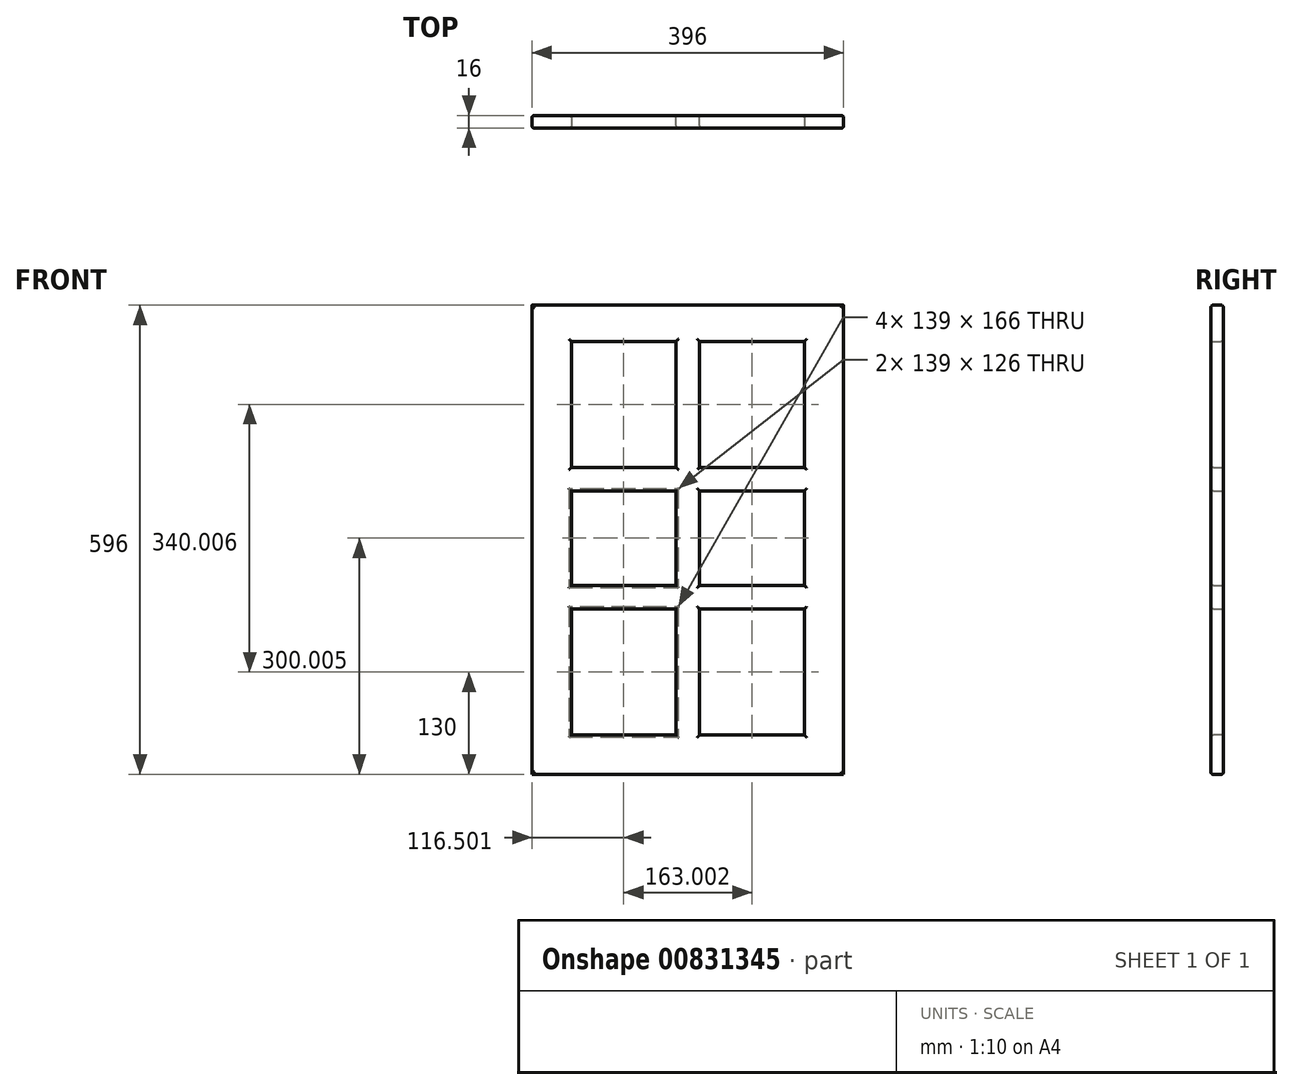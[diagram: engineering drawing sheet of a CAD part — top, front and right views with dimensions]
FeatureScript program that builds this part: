
annotation { "Feature Type Name" : "Feature", "Feature Type Description" : "" }
export const myFeature = defineFeature(function(context is Context, id is Id, definition is map)
    precondition{}
    {
        {
            var Q0;
            Q0=qCreatedBy(makeId("Front.planeOp"),FACE);
            var sketch = newSketch(context, id + "F0", { "sketchPlane" : qUnion([Q0])});
            skLineSegment(sketch, "E0.bottom", {"start": v(0, 0) * mm, "end": v(28.85, 0) * mm});
            skLineSegment(sketch, "E0.top", {"start": v(0, 37.88) * mm, "end": v(28.85, 37.88) * mm});
            skLineSegment(sketch, "E0.left", {"start": v(0, 0) * mm, "end": v(0, 37.88) * mm});
            skLineSegment(sketch, "E0.right", {"start": v(28.85, 0) * mm, "end": v(28.85, 37.88) * mm});
            skSolve(sketch);
        }
        {
            var Q0;
            Q0=makeQuery(id+"F0.imprint","IMPRINT",FACE,{"disambiguationData":[TD([[makeQuery(id+"F0.imprint","IMPRINT",EDGE,{"derivedFrom":sQuery(id+"F0.wireOp",EDGE,"E0.bottom")}),1.0]])]});
            extrude(context, id + "F1", {"entities" : qUnion([Q0]), "depth" : 16 * mm, "offsetDistance" : 25.4 * mm});
        }
        {
            var Q0;
            Q0=makeQuery(id+"F1.opExtrude","SWEPT_FACE",FACE,{"disambiguationData":[OSD([sQuery(id+"F0.wireOp",EDGE,"E0.left")])]});
            extrude(context, id + "F2", {"entities" : qUnion([Q0]), "operationType" : NewBodyOperationType.ADD, "oppositeDirection" : true, "depth" : 296 * mm, "offsetDistance" : 25.4 * mm});
        }
        {
            var Q0;
            {var subQ0=sQuery(id+"F0.wireOp",EDGE,"E0.bottom");Q0=makeQuery(id+"F2.boolean.opBoolean","MERGE",FACE,{"derivedFrom":[makeQuery(id+"F1.opExtrude","SWEPT_FACE",FACE,{"disambiguationData":[OSD([subQ0])]}),makeQuery(id+"F2.opExtrude","SWEPT_FACE",FACE,{"disambiguationData":[OSD([subQ0,sQuery(id+"F0.wireOp",EDGE,"E0.left")])]})]});}
            extrude(context, id + "F3", {"entities" : qUnion([Q0]), "operationType" : NewBodyOperationType.ADD, "oppositeDirection" : true, "depth" : 996 * mm, "offsetDistance" : 25 * mm});
        }
        {
            var Q0;
            {var subQ0=sQuery(id+"F0.wireOp",EDGE,"E0.left");var subQ1=sQuery(id+"F0.wireOp",EDGE,"E0.bottom");Q0=makeQuery(id+"F3.boolean.opBoolean","MERGE",FACE,{"derivedFrom":[makeQuery(id+"F2.boolean.opBoolean","MERGE",FACE,{"derivedFrom":[makeQuery(id+"F1.opExtrude","CAP_FACE",FACE,{"disambiguationData":[OSD([subQ1,sQuery(id+"F0.wireOp",EDGE,"E0.top"),subQ0,sQuery(id+"F0.wireOp",EDGE,"E0.right")])],"isStart":false}),makeQuery(id+"F2.opExtrude","SWEPT_FACE",FACE,{"disambiguationData":[OSD([subQ0]),TDD([makeQuery(id+"F1.opExtrude","CAP_EDGE",EDGE,{"disambiguationData":[OSD([subQ0])],"isStart":false})])]})]}),makeQuery(id+"F3.opExtrude","SWEPT_FACE",FACE,{"disambiguationData":[OSD([subQ1,subQ0]),TDD([makeQuery(id+"F2.boolean.opBoolean","MERGE",EDGE,{"derivedFrom":[makeQuery(id+"F1.opExtrude","CAP_EDGE",EDGE,{"disambiguationData":[OSD([subQ1])],"isStart":false}),makeQuery(id+"F2.opExtrude","SWEPT_EDGE",EDGE,{"disambiguationData":[OSD([subQ1,subQ0]),TDD([makeQuery(id+"F1.opExtrude","CAP_VERTEX",VERTEX,{"disambiguationData":[OSD([subQ1,subQ0])],"isStart":false})])]})]})])]})]});}
            var sketch = newSketch(context, id + "F4", { "sketchPlane" : qUnion([Q0])});
            skLineSegment(sketch, "E1.bottom", {"start": v(48.4, 906.79) * mm, "end": v(248.24, 906.79) * mm});
            skLineSegment(sketch, "E1.top", {"start": v(48.4, 105.66) * mm, "end": v(248.24, 105.66) * mm});
            skLineSegment(sketch, "E1.left", {"start": v(48.4, 906.79) * mm, "end": v(48.4, 105.66) * mm});
            skLineSegment(sketch, "E1.right", {"start": v(248.24, 906.79) * mm, "end": v(248.24, 105.66) * mm});
            skSolve(sketch);
        }
        {
            var Q0;
            Q0=makeQuery(id+"F4.imprint","IMPRINT",FACE,{"disambiguationData":[TD([[makeQuery(id+"F4.imprint","IMPRINT",EDGE,{"derivedFrom":sQuery(id+"F4.wireOp",EDGE,"E1.bottom")}),-1.0]])]});
            extrude(context, id + "F5", {"entities" : qUnion([Q0]), "operationType" : NewBodyOperationType.REMOVE, "oppositeDirection" : true, "depth" : 5 * mm, "offsetDistance" : 25 * mm});
        }
        {
            var Q0;
            Q0=makeQuery(id+"F5.boolean.opBoolean","COPY",FACE,{"derivedFrom":makeQuery(id+"F5.opExtrude","SWEPT_FACE",FACE,{"disambiguationData":[OSD([sQuery(id+"F4.wireOp",EDGE,"E1.bottom")])]})});
            extrude(context, id + "F6", {"entities" : qUnion([Q0]), "operationType" : NewBodyOperationType.REMOVE, "oppositeDirection" : true, "depth" : 39.2 * mm, "offsetDistance" : 25 * mm});
        }
        {
            var Q0;
            {var subQ0=sQuery(id+"F4.wireOp",EDGE,"E1.right");Q0=makeQuery(id+"F6.boolean.opBoolean","MERGE",FACE,{"derivedFrom":[makeQuery(id+"F5.boolean.opBoolean","COPY",FACE,{"derivedFrom":makeQuery(id+"F5.opExtrude","SWEPT_FACE",FACE,{"disambiguationData":[OSD([subQ0])]})}),makeQuery(id+"F6.opExtrude","SWEPT_FACE",FACE,{"disambiguationData":[OSD([sQuery(id+"F4.wireOp",EDGE,"E1.bottom"),subQ0])]})]});}
            extrude(context, id + "F7", {"entities" : qUnion([Q0]), "operationType" : NewBodyOperationType.ADD, "depth" : 2.24 * mm, "offsetDistance" : 25 * mm});
        }
        {
            var Q0;
            Q0=makeQuery(id+"F5.boolean.opBoolean","COPY",FACE,{"derivedFrom":makeQuery(id+"F5.opExtrude","SWEPT_FACE",FACE,{"disambiguationData":[OSD([sQuery(id+"F4.wireOp",EDGE,"E1.top")])]})});
            extrude(context, id + "F8", {"entities" : qUnion([Q0]), "operationType" : NewBodyOperationType.REMOVE, "oppositeDirection" : true, "depth" : 55.66 * mm, "offsetDistance" : 25 * mm});
        }
        {
            var Q0;
            {var subQ0=sQuery(id+"F4.wireOp",EDGE,"E1.left");Q0=makeQuery(id+"F8.boolean.opBoolean","MERGE",FACE,{"derivedFrom":[makeQuery(id+"F6.boolean.opBoolean","MERGE",FACE,{"derivedFrom":[makeQuery(id+"F5.boolean.opBoolean","COPY",FACE,{"derivedFrom":makeQuery(id+"F5.opExtrude","SWEPT_FACE",FACE,{"disambiguationData":[OSD([subQ0])]})}),makeQuery(id+"F6.opExtrude","SWEPT_FACE",FACE,{"disambiguationData":[OSD([sQuery(id+"F4.wireOp",EDGE,"E1.bottom"),subQ0])]})]}),makeQuery(id+"F8.opExtrude","SWEPT_FACE",FACE,{"disambiguationData":[OSD([sQuery(id+"F4.wireOp",EDGE,"E1.top"),subQ0])]})]});}
            extrude(context, id + "F9", {"entities" : qUnion([Q0]), "operationType" : NewBodyOperationType.ADD, "depth" : 1.59 * mm, "offsetDistance" : 25 * mm});
        }
        {
            var Q0;
            {var subQ0=sQuery(id+"F4.wireOp",EDGE,"E1.top");var subQ1=sQuery(id+"F4.wireOp",EDGE,"E1.bottom");Q0=makeQuery(id+"F8.boolean.opBoolean","MERGE",FACE,{"derivedFrom":[makeQuery(id+"F6.boolean.opBoolean","MERGE",FACE,{"derivedFrom":[makeQuery(id+"F5.boolean.opBoolean","COPY",FACE,{"derivedFrom":makeQuery(id+"F5.opExtrude","CAP_FACE",FACE,{"disambiguationData":[OSD([subQ1,subQ0,sQuery(id+"F4.wireOp",EDGE,"E1.left"),sQuery(id+"F4.wireOp",EDGE,"E1.right")])],"isStart":false})}),makeQuery(id+"F6.opExtrude","SWEPT_FACE",FACE,{"disambiguationData":[OSD([subQ1]),TDD([makeQuery(id+"F5.boolean.opBoolean","COPY",EDGE,{"derivedFrom":makeQuery(id+"F5.opExtrude","CAP_EDGE",EDGE,{"disambiguationData":[OSD([subQ1])],"isStart":false})})])]})]}),makeQuery(id+"F8.opExtrude","SWEPT_FACE",FACE,{"disambiguationData":[OSD([subQ0]),TDD([makeQuery(id+"F5.boolean.opBoolean","COPY",EDGE,{"derivedFrom":makeQuery(id+"F5.opExtrude","CAP_EDGE",EDGE,{"disambiguationData":[OSD([subQ0])],"isStart":false})})])]})]});}
            var sketch = newSketch(context, id + "F10", { "sketchPlane" : qUnion([Q0])});
            skLineSegment(sketch, "E2.bottom", {"start": v(127.14, 946) * mm, "end": v(181.91, 946) * mm});
            skLineSegment(sketch, "E2.top", {"start": v(127.14, 50) * mm, "end": v(181.91, 50) * mm});
            skLineSegment(sketch, "E2.left", {"start": v(127.14, 946) * mm, "end": v(127.14, 50) * mm});
            skLineSegment(sketch, "E2.right", {"start": v(181.91, 946) * mm, "end": v(181.91, 50) * mm});
            skSolve(sketch);
        }
        {
            var Q0;
            Q0=makeQuery(id+"F10.imprint","IMPRINT",FACE,{"disambiguationData":[TD([[makeQuery(id+"F10.imprint","IMPRINT",EDGE,{"derivedFrom":sQuery(id+"F10.wireOp",EDGE,"E2.bottom")}),-1.0]])]});
            extrude(context, id + "F11", {"entities" : qUnion([Q0]), "operationType" : NewBodyOperationType.ADD, "depth" : 5 * mm, "offsetDistance" : 25 * mm});
        }
        {
            var Q0;
            Q0=makeQuery(id+"F11.opExtrude","SWEPT_FACE",FACE,{"disambiguationData":[OSD([sQuery(id+"F10.wireOp",EDGE,"E2.left")])]});
            extrude(context, id + "F12", {"entities" : qUnion([Q0]), "operationType" : NewBodyOperationType.REMOVE, "oppositeDirection" : true, "depth" : 5.86 * mm, "offsetDistance" : 25 * mm});
        }
        {
            var Q0;
            Q0=makeQuery(id+"F11.opExtrude","SWEPT_FACE",FACE,{"disambiguationData":[OSD([sQuery(id+"F10.wireOp",EDGE,"E2.right")])]});
            extrude(context, id + "F13", {"entities" : qUnion([Q0]), "operationType" : NewBodyOperationType.REMOVE, "oppositeDirection" : true, "depth" : 18.91 * mm, "offsetDistance" : 25 * mm});
        }
        {
            var Q0;
            {var subQ0=sQuery(id+"F10.wireOp",EDGE,"E2.left");var subQ1=sQuery(id+"F4.wireOp",EDGE,"E1.bottom");var subQ2=sQuery(id+"F4.wireOp",EDGE,"E1.top");var subQ3=sQuery(id+"F4.wireOp",EDGE,"E1.left");Q0=makeQuery(id+"F12.boolean.opBoolean","MERGE",FACE,{"derivedFrom":[makeQuery(id+"F11.boolean.opBoolean","SPLIT",FACE,{"disambiguationData":[TD([makeQuery(id+"F11.opExtrude","SWEPT_FACE",FACE,{"disambiguationData":[OSD([subQ0])]})])],"derivedFrom":makeQuery(id+"F8.boolean.opBoolean","MERGE",FACE,{"derivedFrom":[makeQuery(id+"F6.boolean.opBoolean","MERGE",FACE,{"derivedFrom":[makeQuery(id+"F5.boolean.opBoolean","COPY",FACE,{"derivedFrom":makeQuery(id+"F5.opExtrude","CAP_FACE",FACE,{"disambiguationData":[OSD([subQ1,subQ2,subQ3,sQuery(id+"F4.wireOp",EDGE,"E1.right")])],"isStart":false})}),makeQuery(id+"F6.opExtrude","SWEPT_FACE",FACE,{"disambiguationData":[OSD([subQ1]),TDD([makeQuery(id+"F5.boolean.opBoolean","COPY",EDGE,{"derivedFrom":makeQuery(id+"F5.opExtrude","CAP_EDGE",EDGE,{"disambiguationData":[OSD([subQ1])],"isStart":false})})])]})]}),makeQuery(id+"F8.opExtrude","SWEPT_FACE",FACE,{"disambiguationData":[OSD([subQ2]),TDD([makeQuery(id+"F5.boolean.opBoolean","COPY",EDGE,{"derivedFrom":makeQuery(id+"F5.opExtrude","CAP_EDGE",EDGE,{"disambiguationData":[OSD([subQ2])],"isStart":false})})])]})]})}),makeQuery(id+"F12.opExtrude","SWEPT_FACE",FACE,{"disambiguationData":[OSD([subQ0]),TDD([makeQuery(id+"F11.opExtrude","CAP_EDGE",EDGE,{"disambiguationData":[OSD([subQ0])],"isStart":true})])]})]});}
            var sketch = newSketch(context, id + "F14", { "sketchPlane" : qUnion([Q0])});
            skLineSegment(sketch, "E3.bottom", {"start": v(50, 870.78) * mm, "end": v(133, 870.78) * mm});
            skLineSegment(sketch, "E3.top", {"start": v(50, 835.83) * mm, "end": v(133, 835.83) * mm});
            skLineSegment(sketch, "E3.left", {"start": v(50, 870.78) * mm, "end": v(50, 835.83) * mm});
            skLineSegment(sketch, "E3.right", {"start": v(133, 870.78) * mm, "end": v(133, 835.83) * mm});
            skLineSegment(sketch, "E4.bottom", {"start": v(50, 539.3) * mm, "end": v(133, 539.3) * mm});
            skLineSegment(sketch, "E4.top", {"start": v(50, 484.02) * mm, "end": v(133, 484.02) * mm});
            skLineSegment(sketch, "E4.left", {"start": v(50, 539.3) * mm, "end": v(50, 484.02) * mm});
            skLineSegment(sketch, "E4.right", {"start": v(133, 539.3) * mm, "end": v(133, 484.02) * mm});
            skSolve(sketch);
        }
        {
            var Q0;
            {var subQ0=sQuery(id+"F10.wireOp",EDGE,"E2.right");var subQ1=sQuery(id+"F4.wireOp",EDGE,"E1.top");var subQ2=sQuery(id+"F4.wireOp",EDGE,"E1.right");var subQ3=sQuery(id+"F4.wireOp",EDGE,"E1.bottom");Q0=makeQuery(id+"F13.boolean.opBoolean","MERGE",FACE,{"derivedFrom":[makeQuery(id+"F11.boolean.opBoolean","SPLIT",FACE,{"disambiguationData":[TD([makeQuery(id+"F11.opExtrude","SWEPT_FACE",FACE,{"disambiguationData":[OSD([subQ0])]})])],"derivedFrom":makeQuery(id+"F8.boolean.opBoolean","MERGE",FACE,{"derivedFrom":[makeQuery(id+"F6.boolean.opBoolean","MERGE",FACE,{"derivedFrom":[makeQuery(id+"F5.boolean.opBoolean","COPY",FACE,{"derivedFrom":makeQuery(id+"F5.opExtrude","CAP_FACE",FACE,{"disambiguationData":[OSD([subQ3,subQ1,sQuery(id+"F4.wireOp",EDGE,"E1.left"),subQ2])],"isStart":false})}),makeQuery(id+"F6.opExtrude","SWEPT_FACE",FACE,{"disambiguationData":[OSD([subQ3]),TDD([makeQuery(id+"F5.boolean.opBoolean","COPY",EDGE,{"derivedFrom":makeQuery(id+"F5.opExtrude","CAP_EDGE",EDGE,{"disambiguationData":[OSD([subQ3])],"isStart":false})})])]})]}),makeQuery(id+"F8.opExtrude","SWEPT_FACE",FACE,{"disambiguationData":[OSD([subQ1]),TDD([makeQuery(id+"F5.boolean.opBoolean","COPY",EDGE,{"derivedFrom":makeQuery(id+"F5.opExtrude","CAP_EDGE",EDGE,{"disambiguationData":[OSD([subQ1])],"isStart":false})})])]})]})}),makeQuery(id+"F13.opExtrude","SWEPT_FACE",FACE,{"disambiguationData":[OSD([subQ0]),TDD([makeQuery(id+"F11.opExtrude","CAP_EDGE",EDGE,{"disambiguationData":[OSD([subQ0])],"isStart":true})])]})]});}
            var sketch = newSketch(context, id + "F15", { "sketchPlane" : qUnion([Q0])});
            skLineSegment(sketch, "E5.bottom", {"start": v(163, 876.14) * mm, "end": v(246, 876.14) * mm});
            skLineSegment(sketch, "E5.top", {"start": v(163, 831.26) * mm, "end": v(246, 831.26) * mm});
            skLineSegment(sketch, "E5.left", {"start": v(163, 876.14) * mm, "end": v(163, 831.26) * mm});
            skLineSegment(sketch, "E5.right", {"start": v(246, 876.14) * mm, "end": v(246, 831.26) * mm});
            skLineSegment(sketch, "E6.bottom", {"start": v(163, 602.8) * mm, "end": v(246, 602.8) * mm});
            skLineSegment(sketch, "E6.top", {"start": v(163, 550.28) * mm, "end": v(246, 550.28) * mm});
            skLineSegment(sketch, "E6.left", {"start": v(163, 602.8) * mm, "end": v(163, 550.28) * mm});
            skLineSegment(sketch, "E6.right", {"start": v(246, 602.8) * mm, "end": v(246, 550.28) * mm});
            skSolve(sketch);
        }
        {
            var Q0;
            Q0=makeQuery(id+"F14.imprint","IMPRINT",FACE,{"disambiguationData":[TD([[makeQuery(id+"F14.imprint","IMPRINT",EDGE,{"derivedFrom":sQuery(id+"F14.wireOp",EDGE,"E3.bottom")}),-1.0]])]});
            var Q1;
            Q1=makeQuery(id+"F15.imprint","IMPRINT",FACE,{"disambiguationData":[TD([[makeQuery(id+"F15.imprint","IMPRINT",EDGE,{"derivedFrom":sQuery(id+"F15.wireOp",EDGE,"E5.bottom")}),-1.0]])]});
            var Q2;
            Q2=makeQuery(id+"F15.imprint","IMPRINT",FACE,{"disambiguationData":[TD([[makeQuery(id+"F15.imprint","IMPRINT",EDGE,{"derivedFrom":sQuery(id+"F15.wireOp",EDGE,"E6.bottom")}),-1.0]])]});
            var Q3;
            Q3=makeQuery(id+"F14.imprint","IMPRINT",FACE,{"disambiguationData":[TD([[makeQuery(id+"F14.imprint","IMPRINT",EDGE,{"derivedFrom":sQuery(id+"F14.wireOp",EDGE,"E4.bottom")}),-1.0]])]});
            extrude(context, id + "F16", {"entities" : qUnion([Q0, Q1, Q2, Q3]), "operationType" : NewBodyOperationType.ADD, "depth" : 5 * mm, "offsetDistance" : 25 * mm});
        }
        {
            var Q0;
            Q0=makeQuery(id+"F16.opExtrude","SWEPT_FACE",FACE,{"disambiguationData":[OSD([sQuery(id+"F15.wireOp",EDGE,"E6.top")])]});
            var Q1;
            Q1=makeQuery(id+"F16.opExtrude","SWEPT_FACE",FACE,{"disambiguationData":[OSD([sQuery(id+"F14.wireOp",EDGE,"E4.top")])]});
            extrude(context, id + "F17", {"entities" : qUnion([Q0, Q1]), "operationType" : NewBodyOperationType.ADD, "depth" : 300 * mm, "offsetDistance" : 25 * mm});
        }
        {
            var Q0;
            Q0=makeQuery(id+"F16.opExtrude","SWEPT_FACE",FACE,{"disambiguationData":[OSD([sQuery(id+"F14.wireOp",EDGE,"E4.bottom")])]});
            var Q1;
            Q1=makeQuery(id+"F16.opExtrude","SWEPT_FACE",FACE,{"disambiguationData":[OSD([sQuery(id+"F15.wireOp",EDGE,"E6.bottom")])]});
            extrude(context, id + "F18", {"entities" : qUnion([Q0, Q1]), "operationType" : NewBodyOperationType.REMOVE, "oppositeDirection" : true, "depth" : 300 * mm, "offsetDistance" : 25 * mm});
        }
        {
            var Q0;
            Q0=makeQuery(id+"F16.opExtrude","SWEPT_FACE",FACE,{"disambiguationData":[OSD([sQuery(id+"F14.wireOp",EDGE,"E3.top")])]});
            extrude(context, id + "F19", {"entities" : qUnion([Q0]), "operationType" : NewBodyOperationType.ADD, "depth" : 324.8 * mm, "offsetDistance" : 25 * mm});
        }
        {
            var Q0;
            Q0=makeQuery(id+"F16.opExtrude","SWEPT_FACE",FACE,{"disambiguationData":[OSD([sQuery(id+"F14.wireOp",EDGE,"E3.bottom")])]});
            extrude(context, id + "F20", {"entities" : qUnion([Q0]), "operationType" : NewBodyOperationType.REMOVE, "oppositeDirection" : true, "depth" : 324.8 * mm, "offsetDistance" : 25 * mm});
        }
        {
            var Q0;
            Q0=makeQuery(id+"F18.boolean.opBoolean","COPY",FACE,{"derivedFrom":makeQuery(id+"F18.opExtrude","CAP_FACE",FACE,{"disambiguationData":[OSD([sQuery(id+"F14.wireOp",EDGE,"E4.bottom")])],"isStart":false})});
            extrude(context, id + "F21", {"entities" : qUnion([Q0]), "operationType" : NewBodyOperationType.ADD, "depth" : 250 * mm, "offsetDistance" : 25 * mm});
        }
        {
            var Q0;
            Q0=makeQuery(id+"F17.opExtrude","CAP_FACE",FACE,{"disambiguationData":[OSD([sQuery(id+"F14.wireOp",EDGE,"E4.top")])],"isStart":false});
            extrude(context, id + "F22", {"entities" : qUnion([Q0]), "operationType" : NewBodyOperationType.REMOVE, "oppositeDirection" : true, "depth" : 250 * mm, "offsetDistance" : 25 * mm});
        }
        {
            var Q0;
            Q0=makeQuery(id+"F20.boolean.opBoolean","COPY",FACE,{"derivedFrom":makeQuery(id+"F20.opExtrude","CAP_FACE",FACE,{"disambiguationData":[OSD([sQuery(id+"F14.wireOp",EDGE,"E3.bottom")])],"isStart":false})});
            extrude(context, id + "F23", {"entities" : qUnion([Q0]), "operationType" : NewBodyOperationType.ADD, "depth" : 100 * mm, "offsetDistance" : 25 * mm});
        }
        {
            var Q0;
            Q0=makeQuery(id+"F19.opExtrude","CAP_FACE",FACE,{"disambiguationData":[OSD([sQuery(id+"F14.wireOp",EDGE,"E3.top")])],"isStart":false});
            extrude(context, id + "F24", {"entities" : qUnion([Q0]), "operationType" : NewBodyOperationType.REMOVE, "oppositeDirection" : true, "depth" : 100 * mm, "offsetDistance" : 25 * mm});
        }
        {
            var Q0;
            Q0=makeQuery(id+"F23.opExtrude","CAP_FACE",FACE,{"disambiguationData":[OSD([sQuery(id+"F14.wireOp",EDGE,"E3.bottom")])],"isStart":false});
            extrude(context, id + "F25", {"entities" : qUnion([Q0]), "operationType" : NewBodyOperationType.ADD, "depth" : 50 * mm, "offsetDistance" : 25 * mm});
        }
        {
            var Q0;
            Q0=makeQuery(id+"F24.boolean.opBoolean","COPY",FACE,{"derivedFrom":makeQuery(id+"F24.opExtrude","CAP_FACE",FACE,{"disambiguationData":[OSD([sQuery(id+"F14.wireOp",EDGE,"E3.top")])],"isStart":false})});
            extrude(context, id + "F26", {"entities" : qUnion([Q0]), "operationType" : NewBodyOperationType.REMOVE, "oppositeDirection" : true, "depth" : 50 * mm, "offsetDistance" : 25 * mm});
        }
        {
            var Q0;
            Q0=makeQuery(id+"F22.boolean.opBoolean","COPY",FACE,{"derivedFrom":makeQuery(id+"F22.opExtrude","CAP_FACE",FACE,{"disambiguationData":[OSD([sQuery(id+"F14.wireOp",EDGE,"E4.top")])],"isStart":false})});
            extrude(context, id + "F27", {"entities" : qUnion([Q0]), "operationType" : NewBodyOperationType.ADD, "depth" : 134.02 * mm, "offsetDistance" : 25 * mm});
        }
        {
            var Q0;
            Q0=makeQuery(id+"F27.opExtrude","CAP_FACE",FACE,{"disambiguationData":[OSD([sQuery(id+"F14.wireOp",EDGE,"E4.top")])],"isStart":false});
            extrude(context, id + "F28", {"entities" : qUnion([Q0]), "operationType" : NewBodyOperationType.REMOVE, "oppositeDirection" : true, "depth" : 100 * mm, "offsetDistance" : 25 * mm});
        }
        {
            var Q0;
            Q0=makeQuery(id+"F26.boolean.opBoolean","COPY",FACE,{"derivedFrom":makeQuery(id+"F26.opExtrude","CAP_FACE",FACE,{"disambiguationData":[OSD([sQuery(id+"F14.wireOp",EDGE,"E3.top")])],"isStart":false})});
            extrude(context, id + "F29", {"entities" : qUnion([Q0]), "operationType" : NewBodyOperationType.ADD, "depth" : 100 * mm, "offsetDistance" : 25 * mm});
        }
        {
            var Q0;
            Q0=makeQuery(id+"F25.opExtrude","CAP_FACE",FACE,{"disambiguationData":[OSD([sQuery(id+"F14.wireOp",EDGE,"E3.bottom")])],"isStart":false});
            extrude(context, id + "F30", {"entities" : qUnion([Q0]), "operationType" : NewBodyOperationType.REMOVE, "oppositeDirection" : true, "depth" : 100 * mm, "offsetDistance" : 25 * mm});
        }
        {
            var Q0;
            Q0=makeQuery(id+"F30.boolean.opBoolean","COPY",FACE,{"derivedFrom":makeQuery(id+"F30.opExtrude","CAP_FACE",FACE,{"disambiguationData":[OSD([sQuery(id+"F14.wireOp",EDGE,"E3.bottom")])],"isStart":false})});
            extrude(context, id + "F31", {"entities" : qUnion([Q0]), "operationType" : NewBodyOperationType.ADD, "depth" : 50 * mm, "offsetDistance" : 25 * mm});
        }
        {
            var Q0;
            Q0=makeQuery(id+"F29.opExtrude","CAP_FACE",FACE,{"disambiguationData":[OSD([sQuery(id+"F14.wireOp",EDGE,"E3.top")])],"isStart":false});
            extrude(context, id + "F32", {"entities" : qUnion([Q0]), "operationType" : NewBodyOperationType.REMOVE, "oppositeDirection" : true, "depth" : 54.95 * mm, "offsetDistance" : 25 * mm});
        }
        {
            var Q0;
            Q0=makeQuery(id+"F28.boolean.opBoolean","COPY",FACE,{"derivedFrom":makeQuery(id+"F28.opExtrude","CAP_FACE",FACE,{"disambiguationData":[OSD([sQuery(id+"F14.wireOp",EDGE,"E4.top")])],"isStart":false})});
            extrude(context, id + "F33", {"entities" : qUnion([Q0]), "operationType" : NewBodyOperationType.ADD, "depth" : 50 * mm, "offsetDistance" : 25 * mm});
        }
        {
            var Q0;
            Q0=makeQuery(id+"F21.opExtrude","CAP_FACE",FACE,{"disambiguationData":[OSD([sQuery(id+"F14.wireOp",EDGE,"E4.bottom")])],"isStart":false});
            extrude(context, id + "F34", {"entities" : qUnion([Q0]), "operationType" : NewBodyOperationType.REMOVE, "oppositeDirection" : true, "depth" : 109.3 * mm, "offsetDistance" : 25 * mm});
        }
        {
            var Q0;
            Q0=makeQuery(id+"F16.opExtrude","SWEPT_FACE",FACE,{"disambiguationData":[OSD([sQuery(id+"F15.wireOp",EDGE,"E5.top")])]});
            extrude(context, id + "F35", {"entities" : qUnion([Q0]), "operationType" : NewBodyOperationType.REMOVE, "oppositeDirection" : true, "depth" : 14.88 * mm, "offsetDistance" : 25 * mm});
        }
        {
            var Q0;
            Q0=makeQuery(id+"F35.boolean.opBoolean","COPY",FACE,{"derivedFrom":makeQuery(id+"F35.opExtrude","CAP_FACE",FACE,{"disambiguationData":[OSD([sQuery(id+"F15.wireOp",EDGE,"E5.top")])],"isStart":false})});
            extrude(context, id + "F36", {"entities" : qUnion([Q0]), "operationType" : NewBodyOperationType.ADD, "depth" : 230.15 * mm, "offsetDistance" : 25 * mm});
        }
        {
            var Q0;
            Q0=makeQuery(id+"F16.opExtrude","SWEPT_FACE",FACE,{"disambiguationData":[OSD([sQuery(id+"F15.wireOp",EDGE,"E5.bottom")])]});
            extrude(context, id + "F37", {"entities" : qUnion([Q0]), "operationType" : NewBodyOperationType.REMOVE, "oppositeDirection" : true, "depth" : 230.15 * mm, "offsetDistance" : 25 * mm});
        }
        {
            var Q0;
            Q0=makeQuery(id+"F17.opExtrude","CAP_FACE",FACE,{"disambiguationData":[OSD([sQuery(id+"F15.wireOp",EDGE,"E6.top")])],"isStart":false});
            extrude(context, id + "F38", {"entities" : qUnion([Q0]), "operationType" : NewBodyOperationType.REMOVE, "oppositeDirection" : true, "depth" : 22.52 * mm, "offsetDistance" : 25 * mm});
        }
        {
            var Q0;
            Q0=makeQuery(id+"F18.boolean.opBoolean","COPY",FACE,{"derivedFrom":makeQuery(id+"F18.opExtrude","CAP_FACE",FACE,{"disambiguationData":[OSD([sQuery(id+"F15.wireOp",EDGE,"E6.bottom")])],"isStart":false})});
            extrude(context, id + "F39", {"entities" : qUnion([Q0]), "operationType" : NewBodyOperationType.ADD, "depth" : 77.2 * mm, "offsetDistance" : 25 * mm});
        }
        {
            var Q0;
            Q0=makeQuery(id+"F38.boolean.opBoolean","COPY",FACE,{"derivedFrom":makeQuery(id+"F38.opExtrude","CAP_FACE",FACE,{"disambiguationData":[OSD([sQuery(id+"F15.wireOp",EDGE,"E6.top")])],"isStart":false})});
            extrude(context, id + "F40", {"entities" : qUnion([Q0]), "operationType" : NewBodyOperationType.REMOVE, "oppositeDirection" : true, "depth" : 77.2 * mm, "offsetDistance" : 25 * mm});
        }
        {
            var Q0;
            {var subQ0=sQuery(id+"F14.wireOp",EDGE,"E3.bottom");var subQ1=makeQuery(id+"F16.opExtrude","CAP_EDGE",EDGE,{"disambiguationData":[OSD([subQ0])],"isStart":true});var subQ2=sQuery(id+"F10.wireOp",EDGE,"E2.left");var subQ3=sQuery(id+"F4.wireOp",EDGE,"E1.bottom");var subQ4=sQuery(id+"F4.wireOp",EDGE,"E1.left");var subQ5=sQuery(id+"F4.wireOp",EDGE,"E1.top");var subQ7=makeQuery(id+"F6.boolean.opBoolean","COPY",FACE,{"derivedFrom":makeQuery(id+"F6.opExtrude","CAP_FACE",FACE,{"disambiguationData":[OSD([subQ3])],"isStart":false})});Q0=makeQuery(id+"F30.boolean.opBoolean","MERGE",FACE,{"derivedFrom":[makeQuery(id+"F20.boolean.opBoolean","MERGE",FACE,{"derivedFrom":[makeQuery(id+"F16.boolean.opBoolean","SPLIT",FACE,{"disambiguationData":[TD([subQ7])],"derivedFrom":makeQuery(id+"F12.boolean.opBoolean","MERGE",FACE,{"derivedFrom":[makeQuery(id+"F11.boolean.opBoolean","SPLIT",FACE,{"disambiguationData":[TD([makeQuery(id+"F11.opExtrude","SWEPT_FACE",FACE,{"disambiguationData":[OSD([subQ2])]})])],"derivedFrom":makeQuery(id+"F8.boolean.opBoolean","MERGE",FACE,{"derivedFrom":[makeQuery(id+"F6.boolean.opBoolean","MERGE",FACE,{"derivedFrom":[makeQuery(id+"F5.boolean.opBoolean","COPY",FACE,{"derivedFrom":makeQuery(id+"F5.opExtrude","CAP_FACE",FACE,{"disambiguationData":[OSD([subQ3,subQ5,subQ4,sQuery(id+"F4.wireOp",EDGE,"E1.right")])],"isStart":false})}),makeQuery(id+"F6.opExtrude","SWEPT_FACE",FACE,{"disambiguationData":[OSD([subQ3]),TDD([makeQuery(id+"F5.boolean.opBoolean","COPY",EDGE,{"derivedFrom":makeQuery(id+"F5.opExtrude","CAP_EDGE",EDGE,{"disambiguationData":[OSD([subQ3])],"isStart":false})})])]})]}),makeQuery(id+"F8.opExtrude","SWEPT_FACE",FACE,{"disambiguationData":[OSD([subQ5]),TDD([makeQuery(id+"F5.boolean.opBoolean","COPY",EDGE,{"derivedFrom":makeQuery(id+"F5.opExtrude","CAP_EDGE",EDGE,{"disambiguationData":[OSD([subQ5])],"isStart":false})})])]})]})}),makeQuery(id+"F12.opExtrude","SWEPT_FACE",FACE,{"disambiguationData":[OSD([subQ2]),TDD([makeQuery(id+"F11.opExtrude","CAP_EDGE",EDGE,{"disambiguationData":[OSD([subQ2])],"isStart":true})])]})]})}),makeQuery(id+"F20.opExtrude","SWEPT_FACE",FACE,{"disambiguationData":[OSD([subQ0]),TDD([subQ1])]})]}),makeQuery(id+"F30.opExtrude","SWEPT_FACE",FACE,{"disambiguationData":[OSD([subQ0]),TDD([makeQuery(id+"F25.opExtrude","CAP_EDGE",EDGE,{"disambiguationData":[OSD([subQ0]),TDD([makeQuery(id+"F23.opExtrude","CAP_EDGE",EDGE,{"disambiguationData":[OSD([subQ0]),TDD([makeQuery(id+"F20.boolean.opBoolean","COPY",EDGE,{"derivedFrom":makeQuery(id+"F20.opExtrude","CAP_EDGE",EDGE,{"disambiguationData":[OSD([subQ0]),TDD([subQ1])],"isStart":false})})])],"isStart":false})])],"isStart":false})])]})]});}
            var Q1;
            {var subQ0=sQuery(id+"F15.wireOp",EDGE,"E5.bottom");var subQ1=sQuery(id+"F10.wireOp",EDGE,"E2.right");var subQ2=sQuery(id+"F4.wireOp",EDGE,"E1.bottom");var subQ3=sQuery(id+"F4.wireOp",EDGE,"E1.right");var subQ4=sQuery(id+"F4.wireOp",EDGE,"E1.top");var subQ7=makeQuery(id+"F6.boolean.opBoolean","COPY",FACE,{"derivedFrom":makeQuery(id+"F6.opExtrude","CAP_FACE",FACE,{"disambiguationData":[OSD([subQ2])],"isStart":false})});Q1=makeQuery(id+"F37.boolean.opBoolean","MERGE",FACE,{"derivedFrom":[makeQuery(id+"F16.boolean.opBoolean","SPLIT",FACE,{"disambiguationData":[TD([subQ7])],"derivedFrom":makeQuery(id+"F13.boolean.opBoolean","MERGE",FACE,{"derivedFrom":[makeQuery(id+"F11.boolean.opBoolean","SPLIT",FACE,{"disambiguationData":[TD([makeQuery(id+"F11.opExtrude","SWEPT_FACE",FACE,{"disambiguationData":[OSD([subQ1])]})])],"derivedFrom":makeQuery(id+"F8.boolean.opBoolean","MERGE",FACE,{"derivedFrom":[makeQuery(id+"F6.boolean.opBoolean","MERGE",FACE,{"derivedFrom":[makeQuery(id+"F5.boolean.opBoolean","COPY",FACE,{"derivedFrom":makeQuery(id+"F5.opExtrude","CAP_FACE",FACE,{"disambiguationData":[OSD([subQ2,subQ4,sQuery(id+"F4.wireOp",EDGE,"E1.left"),subQ3])],"isStart":false})}),makeQuery(id+"F6.opExtrude","SWEPT_FACE",FACE,{"disambiguationData":[OSD([subQ2]),TDD([makeQuery(id+"F5.boolean.opBoolean","COPY",EDGE,{"derivedFrom":makeQuery(id+"F5.opExtrude","CAP_EDGE",EDGE,{"disambiguationData":[OSD([subQ2])],"isStart":false})})])]})]}),makeQuery(id+"F8.opExtrude","SWEPT_FACE",FACE,{"disambiguationData":[OSD([subQ4]),TDD([makeQuery(id+"F5.boolean.opBoolean","COPY",EDGE,{"derivedFrom":makeQuery(id+"F5.opExtrude","CAP_EDGE",EDGE,{"disambiguationData":[OSD([subQ4])],"isStart":false})})])]})]})}),makeQuery(id+"F13.opExtrude","SWEPT_FACE",FACE,{"disambiguationData":[OSD([subQ1]),TDD([makeQuery(id+"F11.opExtrude","CAP_EDGE",EDGE,{"disambiguationData":[OSD([subQ1])],"isStart":true})])]})]})}),makeQuery(id+"F37.opExtrude","SWEPT_FACE",FACE,{"disambiguationData":[OSD([subQ0]),TDD([makeQuery(id+"F16.opExtrude","CAP_EDGE",EDGE,{"disambiguationData":[OSD([subQ0])],"isStart":true})])]})]});}
            var Q2;
            {var subQ0=sQuery(id+"F15.wireOp",EDGE,"E5.top");var subQ1=sQuery(id+"F15.wireOp",EDGE,"E6.bottom");var subQ2=sQuery(id+"F10.wireOp",EDGE,"E2.right");var subQ3=sQuery(id+"F4.wireOp",EDGE,"E1.right");var subQ4=sQuery(id+"F4.wireOp",EDGE,"E1.top");var subQ6=sQuery(id+"F4.wireOp",EDGE,"E1.bottom");Q2=makeQuery(id+"F35.boolean.opBoolean","MERGE",FACE,{"derivedFrom":[makeQuery(id+"F18.boolean.opBoolean","MERGE",FACE,{"derivedFrom":[makeQuery(id+"F16.boolean.opBoolean","SPLIT",FACE,{"disambiguationData":[TD([makeQuery(id+"F16.opExtrude","SWEPT_FACE",FACE,{"disambiguationData":[OSD([subQ0])]})])],"derivedFrom":makeQuery(id+"F13.boolean.opBoolean","MERGE",FACE,{"derivedFrom":[makeQuery(id+"F11.boolean.opBoolean","SPLIT",FACE,{"disambiguationData":[TD([makeQuery(id+"F11.opExtrude","SWEPT_FACE",FACE,{"disambiguationData":[OSD([subQ2])]})])],"derivedFrom":makeQuery(id+"F8.boolean.opBoolean","MERGE",FACE,{"derivedFrom":[makeQuery(id+"F6.boolean.opBoolean","MERGE",FACE,{"derivedFrom":[makeQuery(id+"F5.boolean.opBoolean","COPY",FACE,{"derivedFrom":makeQuery(id+"F5.opExtrude","CAP_FACE",FACE,{"disambiguationData":[OSD([subQ6,subQ4,sQuery(id+"F4.wireOp",EDGE,"E1.left"),subQ3])],"isStart":false})}),makeQuery(id+"F6.opExtrude","SWEPT_FACE",FACE,{"disambiguationData":[OSD([subQ6]),TDD([makeQuery(id+"F5.boolean.opBoolean","COPY",EDGE,{"derivedFrom":makeQuery(id+"F5.opExtrude","CAP_EDGE",EDGE,{"disambiguationData":[OSD([subQ6])],"isStart":false})})])]})]}),makeQuery(id+"F8.opExtrude","SWEPT_FACE",FACE,{"disambiguationData":[OSD([subQ4]),TDD([makeQuery(id+"F5.boolean.opBoolean","COPY",EDGE,{"derivedFrom":makeQuery(id+"F5.opExtrude","CAP_EDGE",EDGE,{"disambiguationData":[OSD([subQ4])],"isStart":false})})])]})]})}),makeQuery(id+"F13.opExtrude","SWEPT_FACE",FACE,{"disambiguationData":[OSD([subQ2]),TDD([makeQuery(id+"F11.opExtrude","CAP_EDGE",EDGE,{"disambiguationData":[OSD([subQ2])],"isStart":true})])]})]})}),makeQuery(id+"F18.opExtrude","SWEPT_FACE",FACE,{"disambiguationData":[OSD([subQ1]),TDD([makeQuery(id+"F16.opExtrude","CAP_EDGE",EDGE,{"disambiguationData":[OSD([subQ1])],"isStart":true})])]})]}),makeQuery(id+"F35.opExtrude","SWEPT_FACE",FACE,{"disambiguationData":[OSD([subQ0]),TDD([makeQuery(id+"F16.opExtrude","CAP_EDGE",EDGE,{"disambiguationData":[OSD([subQ0])],"isStart":true})])]})]});}
            var Q3;
            {var subQ0=sQuery(id+"F14.wireOp",EDGE,"E4.bottom");var subQ1=makeQuery(id+"F16.opExtrude","CAP_EDGE",EDGE,{"disambiguationData":[OSD([subQ0])],"isStart":true});var subQ2=sQuery(id+"F14.wireOp",EDGE,"E3.top");var subQ3=makeQuery(id+"F19.opExtrude","CAP_EDGE",EDGE,{"disambiguationData":[OSD([subQ2]),TDD([makeQuery(id+"F16.opExtrude","CAP_EDGE",EDGE,{"disambiguationData":[OSD([subQ2])],"isStart":true})])],"isStart":false});var subQ4=makeQuery(id+"F24.boolean.opBoolean","COPY",EDGE,{"derivedFrom":makeQuery(id+"F24.opExtrude","CAP_EDGE",EDGE,{"disambiguationData":[OSD([subQ2]),TDD([subQ3])],"isStart":false})});var subQ5=sQuery(id+"F4.wireOp",EDGE,"E1.left");var subQ6=sQuery(id+"F4.wireOp",EDGE,"E1.top");var subQ7=sQuery(id+"F4.wireOp",EDGE,"E1.bottom");var subQ9=sQuery(id+"F10.wireOp",EDGE,"E2.left");Q3=makeQuery(id+"F34.boolean.opBoolean","MERGE",FACE,{"derivedFrom":[makeQuery(id+"F32.boolean.opBoolean","MERGE",FACE,{"derivedFrom":[makeQuery(id+"F26.boolean.opBoolean","MERGE",FACE,{"derivedFrom":[makeQuery(id+"F24.boolean.opBoolean","MERGE",FACE,{"derivedFrom":[makeQuery(id+"F18.boolean.opBoolean","MERGE",FACE,{"derivedFrom":[makeQuery(id+"F16.boolean.opBoolean","SPLIT",FACE,{"disambiguationData":[TD([makeQuery(id+"F16.opExtrude","SWEPT_FACE",FACE,{"disambiguationData":[OSD([subQ2])]})])],"derivedFrom":makeQuery(id+"F12.boolean.opBoolean","MERGE",FACE,{"derivedFrom":[makeQuery(id+"F11.boolean.opBoolean","SPLIT",FACE,{"disambiguationData":[TD([makeQuery(id+"F11.opExtrude","SWEPT_FACE",FACE,{"disambiguationData":[OSD([subQ9])]})])],"derivedFrom":makeQuery(id+"F8.boolean.opBoolean","MERGE",FACE,{"derivedFrom":[makeQuery(id+"F6.boolean.opBoolean","MERGE",FACE,{"derivedFrom":[makeQuery(id+"F5.boolean.opBoolean","COPY",FACE,{"derivedFrom":makeQuery(id+"F5.opExtrude","CAP_FACE",FACE,{"disambiguationData":[OSD([subQ7,subQ6,subQ5,sQuery(id+"F4.wireOp",EDGE,"E1.right")])],"isStart":false})}),makeQuery(id+"F6.opExtrude","SWEPT_FACE",FACE,{"disambiguationData":[OSD([subQ7]),TDD([makeQuery(id+"F5.boolean.opBoolean","COPY",EDGE,{"derivedFrom":makeQuery(id+"F5.opExtrude","CAP_EDGE",EDGE,{"disambiguationData":[OSD([subQ7])],"isStart":false})})])]})]}),makeQuery(id+"F8.opExtrude","SWEPT_FACE",FACE,{"disambiguationData":[OSD([subQ6]),TDD([makeQuery(id+"F5.boolean.opBoolean","COPY",EDGE,{"derivedFrom":makeQuery(id+"F5.opExtrude","CAP_EDGE",EDGE,{"disambiguationData":[OSD([subQ6])],"isStart":false})})])]})]})}),makeQuery(id+"F12.opExtrude","SWEPT_FACE",FACE,{"disambiguationData":[OSD([subQ9]),TDD([makeQuery(id+"F11.opExtrude","CAP_EDGE",EDGE,{"disambiguationData":[OSD([subQ9])],"isStart":true})])]})]})}),makeQuery(id+"F18.opExtrude","SWEPT_FACE",FACE,{"disambiguationData":[OSD([subQ0]),TDD([subQ1])]})]}),makeQuery(id+"F24.opExtrude","SWEPT_FACE",FACE,{"disambiguationData":[OSD([subQ2]),TDD([subQ3])]})]}),makeQuery(id+"F26.opExtrude","SWEPT_FACE",FACE,{"disambiguationData":[OSD([subQ2]),TDD([subQ4])]})]}),makeQuery(id+"F32.opExtrude","SWEPT_FACE",FACE,{"disambiguationData":[OSD([subQ2]),TDD([makeQuery(id+"F29.opExtrude","CAP_EDGE",EDGE,{"disambiguationData":[OSD([subQ2]),TDD([makeQuery(id+"F26.boolean.opBoolean","COPY",EDGE,{"derivedFrom":makeQuery(id+"F26.opExtrude","CAP_EDGE",EDGE,{"disambiguationData":[OSD([subQ2]),TDD([subQ4])],"isStart":false})})])],"isStart":false})])]})]}),makeQuery(id+"F34.opExtrude","SWEPT_FACE",FACE,{"disambiguationData":[OSD([subQ0]),TDD([makeQuery(id+"F21.opExtrude","CAP_EDGE",EDGE,{"disambiguationData":[OSD([subQ0]),TDD([makeQuery(id+"F18.boolean.opBoolean","COPY",EDGE,{"derivedFrom":makeQuery(id+"F18.opExtrude","CAP_EDGE",EDGE,{"disambiguationData":[OSD([subQ0]),TDD([subQ1])],"isStart":false})})])],"isStart":false})])]})]});}
            var Q4;
            {var subQ0=sQuery(id+"F14.wireOp",EDGE,"E4.top");var subQ1=makeQuery(id+"F17.opExtrude","CAP_EDGE",EDGE,{"disambiguationData":[OSD([subQ0]),TDD([makeQuery(id+"F16.opExtrude","CAP_EDGE",EDGE,{"disambiguationData":[OSD([subQ0])],"isStart":true})])],"isStart":false});var subQ2=sQuery(id+"F10.wireOp",EDGE,"E2.left");var subQ3=sQuery(id+"F4.wireOp",EDGE,"E1.top");var subQ4=sQuery(id+"F4.wireOp",EDGE,"E1.left");var subQ5=sQuery(id+"F4.wireOp",EDGE,"E1.bottom");var subQ7=makeQuery(id+"F8.boolean.opBoolean","COPY",FACE,{"derivedFrom":makeQuery(id+"F8.opExtrude","CAP_FACE",FACE,{"disambiguationData":[OSD([subQ3])],"isStart":false})});Q4=makeQuery(id+"F28.boolean.opBoolean","MERGE",FACE,{"derivedFrom":[makeQuery(id+"F22.boolean.opBoolean","MERGE",FACE,{"derivedFrom":[makeQuery(id+"F16.boolean.opBoolean","SPLIT",FACE,{"disambiguationData":[TD([subQ7])],"derivedFrom":makeQuery(id+"F12.boolean.opBoolean","MERGE",FACE,{"derivedFrom":[makeQuery(id+"F11.boolean.opBoolean","SPLIT",FACE,{"disambiguationData":[TD([makeQuery(id+"F11.opExtrude","SWEPT_FACE",FACE,{"disambiguationData":[OSD([subQ2])]})])],"derivedFrom":makeQuery(id+"F8.boolean.opBoolean","MERGE",FACE,{"derivedFrom":[makeQuery(id+"F6.boolean.opBoolean","MERGE",FACE,{"derivedFrom":[makeQuery(id+"F5.boolean.opBoolean","COPY",FACE,{"derivedFrom":makeQuery(id+"F5.opExtrude","CAP_FACE",FACE,{"disambiguationData":[OSD([subQ5,subQ3,subQ4,sQuery(id+"F4.wireOp",EDGE,"E1.right")])],"isStart":false})}),makeQuery(id+"F6.opExtrude","SWEPT_FACE",FACE,{"disambiguationData":[OSD([subQ5]),TDD([makeQuery(id+"F5.boolean.opBoolean","COPY",EDGE,{"derivedFrom":makeQuery(id+"F5.opExtrude","CAP_EDGE",EDGE,{"disambiguationData":[OSD([subQ5])],"isStart":false})})])]})]}),makeQuery(id+"F8.opExtrude","SWEPT_FACE",FACE,{"disambiguationData":[OSD([subQ3]),TDD([makeQuery(id+"F5.boolean.opBoolean","COPY",EDGE,{"derivedFrom":makeQuery(id+"F5.opExtrude","CAP_EDGE",EDGE,{"disambiguationData":[OSD([subQ3])],"isStart":false})})])]})]})}),makeQuery(id+"F12.opExtrude","SWEPT_FACE",FACE,{"disambiguationData":[OSD([subQ2]),TDD([makeQuery(id+"F11.opExtrude","CAP_EDGE",EDGE,{"disambiguationData":[OSD([subQ2])],"isStart":true})])]})]})}),makeQuery(id+"F22.opExtrude","SWEPT_FACE",FACE,{"disambiguationData":[OSD([subQ0]),TDD([subQ1])]})]}),makeQuery(id+"F28.opExtrude","SWEPT_FACE",FACE,{"disambiguationData":[OSD([subQ0]),TDD([makeQuery(id+"F27.opExtrude","CAP_EDGE",EDGE,{"disambiguationData":[OSD([subQ0]),TDD([makeQuery(id+"F22.boolean.opBoolean","COPY",EDGE,{"derivedFrom":makeQuery(id+"F22.opExtrude","CAP_EDGE",EDGE,{"disambiguationData":[OSD([subQ0]),TDD([subQ1])],"isStart":false})})])],"isStart":false})])]})]});}
            var Q5;
            {var subQ0=sQuery(id+"F15.wireOp",EDGE,"E6.top");var subQ1=makeQuery(id+"F17.opExtrude","CAP_EDGE",EDGE,{"disambiguationData":[OSD([subQ0]),TDD([makeQuery(id+"F16.opExtrude","CAP_EDGE",EDGE,{"disambiguationData":[OSD([subQ0])],"isStart":true})])],"isStart":false});var subQ2=sQuery(id+"F10.wireOp",EDGE,"E2.right");var subQ3=sQuery(id+"F4.wireOp",EDGE,"E1.top");var subQ4=makeQuery(id+"F8.boolean.opBoolean","COPY",FACE,{"derivedFrom":makeQuery(id+"F8.opExtrude","CAP_FACE",FACE,{"disambiguationData":[OSD([subQ3])],"isStart":false})});var subQ5=sQuery(id+"F4.wireOp",EDGE,"E1.right");var subQ7=sQuery(id+"F4.wireOp",EDGE,"E1.bottom");Q5=makeQuery(id+"F40.boolean.opBoolean","MERGE",FACE,{"derivedFrom":[makeQuery(id+"F38.boolean.opBoolean","MERGE",FACE,{"derivedFrom":[makeQuery(id+"F16.boolean.opBoolean","SPLIT",FACE,{"disambiguationData":[TD([subQ4])],"derivedFrom":makeQuery(id+"F13.boolean.opBoolean","MERGE",FACE,{"derivedFrom":[makeQuery(id+"F11.boolean.opBoolean","SPLIT",FACE,{"disambiguationData":[TD([makeQuery(id+"F11.opExtrude","SWEPT_FACE",FACE,{"disambiguationData":[OSD([subQ2])]})])],"derivedFrom":makeQuery(id+"F8.boolean.opBoolean","MERGE",FACE,{"derivedFrom":[makeQuery(id+"F6.boolean.opBoolean","MERGE",FACE,{"derivedFrom":[makeQuery(id+"F5.boolean.opBoolean","COPY",FACE,{"derivedFrom":makeQuery(id+"F5.opExtrude","CAP_FACE",FACE,{"disambiguationData":[OSD([subQ7,subQ3,sQuery(id+"F4.wireOp",EDGE,"E1.left"),subQ5])],"isStart":false})}),makeQuery(id+"F6.opExtrude","SWEPT_FACE",FACE,{"disambiguationData":[OSD([subQ7]),TDD([makeQuery(id+"F5.boolean.opBoolean","COPY",EDGE,{"derivedFrom":makeQuery(id+"F5.opExtrude","CAP_EDGE",EDGE,{"disambiguationData":[OSD([subQ7])],"isStart":false})})])]})]}),makeQuery(id+"F8.opExtrude","SWEPT_FACE",FACE,{"disambiguationData":[OSD([subQ3]),TDD([makeQuery(id+"F5.boolean.opBoolean","COPY",EDGE,{"derivedFrom":makeQuery(id+"F5.opExtrude","CAP_EDGE",EDGE,{"disambiguationData":[OSD([subQ3])],"isStart":false})})])]})]})}),makeQuery(id+"F13.opExtrude","SWEPT_FACE",FACE,{"disambiguationData":[OSD([subQ2]),TDD([makeQuery(id+"F11.opExtrude","CAP_EDGE",EDGE,{"disambiguationData":[OSD([subQ2])],"isStart":true})])]})]})}),makeQuery(id+"F38.opExtrude","SWEPT_FACE",FACE,{"disambiguationData":[OSD([subQ0]),TDD([subQ1])]})]}),makeQuery(id+"F40.opExtrude","SWEPT_FACE",FACE,{"disambiguationData":[OSD([subQ0]),TDD([makeQuery(id+"F38.boolean.opBoolean","COPY",EDGE,{"derivedFrom":makeQuery(id+"F38.opExtrude","CAP_EDGE",EDGE,{"disambiguationData":[OSD([subQ0]),TDD([subQ1])],"isStart":false})})])]})]});}
            extrude(context, id + "F41", {"entities" : qUnion([Q0, Q1, Q2, Q3, Q4, Q5]), "operationType" : NewBodyOperationType.REMOVE, "oppositeDirection" : true, "depth" : 11 * mm, "offsetDistance" : 25 * mm});
        }
        {
            var Q0;
            {var subQ0=sQuery(id+"F14.wireOp",EDGE,"E4.top");Q0=makeQuery(id+"F41.boolean.opBoolean","MERGE",FACE,{"derivedFrom":[makeQuery(id+"F33.opExtrude","CAP_FACE",FACE,{"disambiguationData":[OSD([subQ0])],"isStart":false}),makeQuery(id+"F41.opExtrude","SWEPT_FACE",FACE,{"disambiguationData":[OSD([subQ0])]})]});}
            var Q1;
            {var subQ0=sQuery(id+"F15.wireOp",EDGE,"E6.top");Q1=makeQuery(id+"F41.boolean.opBoolean","MERGE",FACE,{"derivedFrom":[makeQuery(id+"F40.boolean.opBoolean","COPY",FACE,{"derivedFrom":makeQuery(id+"F40.opExtrude","CAP_FACE",FACE,{"disambiguationData":[OSD([subQ0])],"isStart":false})}),makeQuery(id+"F41.opExtrude","SWEPT_FACE",FACE,{"disambiguationData":[OSD([subQ0])]})]});}
            extrude(context, id + "F42", {"entities" : qUnion([Q0, Q1]), "operationType" : NewBodyOperationType.ADD, "depth" : 100 * mm, "offsetDistance" : 25 * mm});
        }
        {
            var Q0;
            {var subQ0=sQuery(id+"F14.wireOp",EDGE,"E4.bottom");Q0=makeQuery(id+"F41.boolean.opBoolean","MERGE",FACE,{"derivedFrom":[makeQuery(id+"F34.boolean.opBoolean","COPY",FACE,{"derivedFrom":makeQuery(id+"F34.opExtrude","CAP_FACE",FACE,{"disambiguationData":[OSD([subQ0])],"isStart":false})}),makeQuery(id+"F41.opExtrude","SWEPT_FACE",FACE,{"disambiguationData":[OSD([subQ0])]})]});}
            var Q1;
            {var subQ0=sQuery(id+"F15.wireOp",EDGE,"E6.bottom");Q1=makeQuery(id+"F41.boolean.opBoolean","MERGE",FACE,{"derivedFrom":[makeQuery(id+"F39.opExtrude","CAP_FACE",FACE,{"disambiguationData":[OSD([subQ0])],"isStart":false}),makeQuery(id+"F41.opExtrude","SWEPT_FACE",FACE,{"disambiguationData":[OSD([subQ0])]})]});}
            extrude(context, id + "F43", {"entities" : qUnion([Q0, Q1]), "operationType" : NewBodyOperationType.REMOVE, "oppositeDirection" : true, "depth" : 100 * mm, "offsetDistance" : 25 * mm});
        }
        {
            var Q0;
            {var subQ0=sQuery(id+"F14.wireOp",EDGE,"E3.top");Q0=makeQuery(id+"F41.boolean.opBoolean","MERGE",FACE,{"derivedFrom":[makeQuery(id+"F32.boolean.opBoolean","COPY",FACE,{"derivedFrom":makeQuery(id+"F32.opExtrude","CAP_FACE",FACE,{"disambiguationData":[OSD([subQ0])],"isStart":false})}),makeQuery(id+"F41.opExtrude","SWEPT_FACE",FACE,{"disambiguationData":[OSD([subQ0])]})]});}
            var Q1;
            {var subQ0=sQuery(id+"F15.wireOp",EDGE,"E5.top");Q1=makeQuery(id+"F41.boolean.opBoolean","MERGE",FACE,{"derivedFrom":[makeQuery(id+"F36.opExtrude","CAP_FACE",FACE,{"disambiguationData":[OSD([subQ0])],"isStart":false}),makeQuery(id+"F41.opExtrude","SWEPT_FACE",FACE,{"disambiguationData":[OSD([subQ0])]})]});}
            extrude(context, id + "F44", {"entities" : qUnion([Q0, Q1]), "operationType" : NewBodyOperationType.ADD, "depth" : 196 * mm, "offsetDistance" : 25 * mm});
        }
        {
            var Q0;
            {var subQ0=sQuery(id+"F14.wireOp",EDGE,"E3.bottom");Q0=makeQuery(id+"F41.boolean.opBoolean","MERGE",FACE,{"derivedFrom":[makeQuery(id+"F31.opExtrude","CAP_FACE",FACE,{"disambiguationData":[OSD([subQ0])],"isStart":false}),makeQuery(id+"F41.opExtrude","SWEPT_FACE",FACE,{"disambiguationData":[OSD([subQ0])]})]});}
            var Q1;
            {var subQ0=sQuery(id+"F15.wireOp",EDGE,"E5.bottom");Q1=makeQuery(id+"F41.boolean.opBoolean","MERGE",FACE,{"derivedFrom":[makeQuery(id+"F37.boolean.opBoolean","COPY",FACE,{"derivedFrom":makeQuery(id+"F37.opExtrude","CAP_FACE",FACE,{"disambiguationData":[OSD([subQ0])],"isStart":false})}),makeQuery(id+"F41.opExtrude","SWEPT_FACE",FACE,{"disambiguationData":[OSD([subQ0])]})]});}
            extrude(context, id + "F45", {"entities" : qUnion([Q0, Q1]), "operationType" : NewBodyOperationType.REMOVE, "oppositeDirection" : true, "depth" : 196 * mm, "offsetDistance" : 25 * mm});
        }
        {
            var Q0;
            {var subQ0=sQuery(id+"F10.wireOp",EDGE,"E2.left");var subQ1=sQuery(id+"F10.wireOp",EDGE,"E2.bottom");var subQ2=sQuery(id+"F4.wireOp",EDGE,"E1.bottom");Q0=makeQuery(id+"F41.boolean.opBoolean","MERGE",FACE,{"derivedFrom":[makeQuery(id+"F12.boolean.opBoolean","MERGE",FACE,{"derivedFrom":[makeQuery(id+"F11.boolean.opBoolean","SPLIT",FACE,{"disambiguationData":[TD([makeQuery(id+"F11.opExtrude","SWEPT_FACE",FACE,{"disambiguationData":[OSD([subQ0])]})])],"derivedFrom":makeQuery(id+"F6.boolean.opBoolean","COPY",FACE,{"derivedFrom":makeQuery(id+"F6.opExtrude","CAP_FACE",FACE,{"disambiguationData":[OSD([subQ2])],"isStart":false})})}),makeQuery(id+"F12.opExtrude","SWEPT_FACE",FACE,{"disambiguationData":[OSD([subQ2,subQ1,subQ0])]})]}),makeQuery(id+"F41.opExtrude","SWEPT_FACE",FACE,{"disambiguationData":[OSD([subQ2,subQ1,subQ0])]})]});}
            var Q1;
            {var subQ0=sQuery(id+"F10.wireOp",EDGE,"E2.right");var subQ1=sQuery(id+"F10.wireOp",EDGE,"E2.bottom");var subQ2=sQuery(id+"F4.wireOp",EDGE,"E1.bottom");Q1=makeQuery(id+"F41.boolean.opBoolean","MERGE",FACE,{"derivedFrom":[makeQuery(id+"F13.boolean.opBoolean","MERGE",FACE,{"derivedFrom":[makeQuery(id+"F11.boolean.opBoolean","SPLIT",FACE,{"disambiguationData":[TD([makeQuery(id+"F11.opExtrude","SWEPT_FACE",FACE,{"disambiguationData":[OSD([subQ0])]})])],"derivedFrom":makeQuery(id+"F6.boolean.opBoolean","COPY",FACE,{"derivedFrom":makeQuery(id+"F6.opExtrude","CAP_FACE",FACE,{"disambiguationData":[OSD([subQ2])],"isStart":false})})}),makeQuery(id+"F13.opExtrude","SWEPT_FACE",FACE,{"disambiguationData":[OSD([subQ2,subQ1,subQ0])]})]}),makeQuery(id+"F41.opExtrude","SWEPT_FACE",FACE,{"disambiguationData":[OSD([subQ2,subQ1,subQ0])]})]});}
            extrude(context, id + "F46", {"entities" : qUnion([Q0, Q1]), "operationType" : NewBodyOperationType.ADD, "depth" : 296 * mm, "offsetDistance" : 25 * mm});
        }
        {
            var Q0;
            Q0=makeQuery(id+"F3.opExtrude","CAP_FACE",FACE,{"disambiguationData":[OSD([sQuery(id+"F0.wireOp",EDGE,"E0.bottom"),sQuery(id+"F0.wireOp",EDGE,"E0.left")])],"isStart":false});
            extrude(context, id + "F47", {"entities" : qUnion([Q0]), "operationType" : NewBodyOperationType.REMOVE, "oppositeDirection" : true, "depth" : 296 * mm, "offsetDistance" : 25 * mm});
        }
        {
            var Q0;
            Q0=makeQuery(id+"F46.opExtrude","CAP_FACE",FACE,{"disambiguationData":[OSD([sQuery(id+"F4.wireOp",EDGE,"E1.bottom"),sQuery(id+"F10.wireOp",EDGE,"E2.bottom"),sQuery(id+"F10.wireOp",EDGE,"E2.right")])],"isStart":false});
            var Q1;
            Q1=makeQuery(id+"F46.opExtrude","CAP_FACE",FACE,{"disambiguationData":[OSD([sQuery(id+"F4.wireOp",EDGE,"E1.bottom"),sQuery(id+"F10.wireOp",EDGE,"E2.bottom"),sQuery(id+"F10.wireOp",EDGE,"E2.left")])],"isStart":false});
            extrude(context, id + "F48", {"entities" : qUnion([Q0, Q1]), "operationType" : NewBodyOperationType.ADD, "depth" : 100 * mm, "offsetDistance" : 25 * mm});
        }
        {
            var Q0;
            Q0=makeQuery(id+"F47.boolean.opBoolean","COPY",FACE,{"derivedFrom":makeQuery(id+"F47.opExtrude","CAP_FACE",FACE,{"disambiguationData":[OSD([sQuery(id+"F0.wireOp",EDGE,"E0.bottom"),sQuery(id+"F0.wireOp",EDGE,"E0.left")])],"isStart":false})});
            extrude(context, id + "F49", {"entities" : qUnion([Q0]), "operationType" : NewBodyOperationType.REMOVE, "oppositeDirection" : true, "depth" : 104 * mm, "offsetDistance" : 25 * mm});
        }
        {
            var Q0;
            Q0=makeQuery(id+"F42.opExtrude","CAP_FACE",FACE,{"disambiguationData":[OSD([sQuery(id+"F14.wireOp",EDGE,"E4.top")])],"isStart":false});
            extrude(context, id + "F50", {"entities" : qUnion([Q0]), "operationType" : NewBodyOperationType.ADD, "depth" : 20 * mm, "offsetDistance" : 25 * mm});
        }
        {
            var Q0;
            Q0=makeQuery(id+"F42.opExtrude","CAP_FACE",FACE,{"disambiguationData":[OSD([sQuery(id+"F15.wireOp",EDGE,"E6.top")])],"isStart":false});
            extrude(context, id + "F51", {"entities" : qUnion([Q0]), "operationType" : NewBodyOperationType.ADD, "depth" : 20 * mm, "offsetDistance" : 25 * mm});
        }
        {
            var Q0;
            Q0=makeQuery(id+"F43.boolean.opBoolean","COPY",FACE,{"derivedFrom":makeQuery(id+"F43.opExtrude","CAP_FACE",FACE,{"disambiguationData":[OSD([sQuery(id+"F14.wireOp",EDGE,"E4.bottom")])],"isStart":false})});
            var Q1;
            Q1=makeQuery(id+"F43.boolean.opBoolean","COPY",FACE,{"derivedFrom":makeQuery(id+"F43.opExtrude","CAP_FACE",FACE,{"disambiguationData":[OSD([sQuery(id+"F15.wireOp",EDGE,"E6.bottom")])],"isStart":false})});
            extrude(context, id + "F52", {"entities" : qUnion([Q0, Q1]), "operationType" : NewBodyOperationType.REMOVE, "oppositeDirection" : true, "depth" : 20 * mm, "offsetDistance" : 25 * mm});
        }
        {
            var Q0;
            Q0=makeQuery(id+"F44.opExtrude","CAP_FACE",FACE,{"disambiguationData":[OSD([sQuery(id+"F15.wireOp",EDGE,"E5.top")])],"isStart":false});
            var Q1;
            Q1=makeQuery(id+"F44.opExtrude","CAP_FACE",FACE,{"disambiguationData":[OSD([sQuery(id+"F14.wireOp",EDGE,"E3.top")])],"isStart":false});
            extrude(context, id + "F53", {"entities" : qUnion([Q0, Q1]), "operationType" : NewBodyOperationType.ADD, "depth" : 80 * mm, "offsetDistance" : 25 * mm});
        }
        {
            var Q0;
            Q0=makeQuery(id+"F45.boolean.opBoolean","COPY",FACE,{"derivedFrom":makeQuery(id+"F45.opExtrude","CAP_FACE",FACE,{"disambiguationData":[OSD([sQuery(id+"F14.wireOp",EDGE,"E3.bottom")])],"isStart":false})});
            var Q1;
            Q1=makeQuery(id+"F45.boolean.opBoolean","COPY",FACE,{"derivedFrom":makeQuery(id+"F45.opExtrude","CAP_FACE",FACE,{"disambiguationData":[OSD([sQuery(id+"F15.wireOp",EDGE,"E5.bottom")])],"isStart":false})});
            extrude(context, id + "F54", {"entities" : qUnion([Q0, Q1]), "operationType" : NewBodyOperationType.REMOVE, "oppositeDirection" : true, "depth" : 80 * mm, "offsetDistance" : 25 * mm});
        }
        {
            var Q0;
            Q0=makeQuery(id+"F54.boolean.opBoolean","COPY",FACE,{"derivedFrom":makeQuery(id+"F54.opExtrude","CAP_FACE",FACE,{"disambiguationData":[OSD([sQuery(id+"F15.wireOp",EDGE,"E5.bottom")])],"isStart":false})});
            var Q1;
            Q1=makeQuery(id+"F54.boolean.opBoolean","COPY",FACE,{"derivedFrom":makeQuery(id+"F54.opExtrude","CAP_FACE",FACE,{"disambiguationData":[OSD([sQuery(id+"F14.wireOp",EDGE,"E3.bottom")])],"isStart":false})});
            extrude(context, id + "F55", {"entities" : qUnion([Q0, Q1]), "operationType" : NewBodyOperationType.ADD, "depth" : 20 * mm, "offsetDistance" : 25 * mm});
        }
        {
            var Q0;
            Q0=makeQuery(id+"F53.opExtrude","CAP_FACE",FACE,{"disambiguationData":[OSD([sQuery(id+"F14.wireOp",EDGE,"E3.top")])],"isStart":false});
            var Q1;
            Q1=makeQuery(id+"F53.opExtrude","CAP_FACE",FACE,{"disambiguationData":[OSD([sQuery(id+"F15.wireOp",EDGE,"E5.top")])],"isStart":false});
            extrude(context, id + "F56", {"entities" : qUnion([Q0, Q1]), "operationType" : NewBodyOperationType.REMOVE, "oppositeDirection" : true, "depth" : 20 * mm, "offsetDistance" : 25 * mm});
        }
        {
            var Q0;
            Q0=makeQuery(id+"F51.opExtrude","CAP_FACE",FACE,{"disambiguationData":[OSD([sQuery(id+"F15.wireOp",EDGE,"E6.top")])],"isStart":false});
            var Q1;
            Q1=makeQuery(id+"F50.opExtrude","CAP_FACE",FACE,{"disambiguationData":[OSD([sQuery(id+"F14.wireOp",EDGE,"E4.top")])],"isStart":false});
            extrude(context, id + "F57", {"entities" : qUnion([Q0, Q1]), "operationType" : NewBodyOperationType.ADD, "depth" : 20 * mm, "offsetDistance" : 25 * mm});
        }
        {
            var Q0;
            Q0=makeQuery(id+"F52.boolean.opBoolean","COPY",FACE,{"derivedFrom":makeQuery(id+"F52.opExtrude","CAP_FACE",FACE,{"disambiguationData":[OSD([sQuery(id+"F15.wireOp",EDGE,"E6.bottom")])],"isStart":false})});
            var Q1;
            Q1=makeQuery(id+"F52.boolean.opBoolean","COPY",FACE,{"derivedFrom":makeQuery(id+"F52.opExtrude","CAP_FACE",FACE,{"disambiguationData":[OSD([sQuery(id+"F14.wireOp",EDGE,"E4.bottom")])],"isStart":false})});
            extrude(context, id + "F58", {"entities" : qUnion([Q0, Q1]), "operationType" : NewBodyOperationType.REMOVE, "oppositeDirection" : true, "depth" : 20 * mm, "offsetDistance" : 25 * mm});
        }
        {
            var Q0;
            {var subQ0=sQuery(id+"F0.wireOp",EDGE,"E0.left");var subQ1=sQuery(id+"F0.wireOp",EDGE,"E0.bottom");Q0=makeQuery(id+"F3.boolean.opBoolean","MERGE",FACE,{"derivedFrom":[makeQuery(id+"F2.opExtrude","CAP_FACE",FACE,{"disambiguationData":[OSD([subQ0])],"isStart":false}),makeQuery(id+"F3.opExtrude","SWEPT_FACE",FACE,{"disambiguationData":[OSD([subQ1,subQ0]),TDD([makeQuery(id+"F2.opExtrude","CAP_EDGE",EDGE,{"disambiguationData":[OSD([subQ1,subQ0])],"isStart":false})])]})]});}
            extrude(context, id + "F59", {"entities" : qUnion([Q0]), "operationType" : NewBodyOperationType.ADD, "depth" : 100 * mm, "offsetDistance" : 25 * mm});
        }
        {
            var Q0;
            {var subQ0=sQuery(id+"F15.wireOp",EDGE,"E5.right");var subQ1=sQuery(id+"F15.wireOp",EDGE,"E5.bottom");var subQ2=sQuery(id+"F4.wireOp",EDGE,"E1.right");var subQ3=sQuery(id+"F4.wireOp",EDGE,"E1.top");var subQ4=sQuery(id+"F4.wireOp",EDGE,"E1.bottom");Q0=makeQuery(id+"F54.boolean.opBoolean","MERGE",FACE,{"derivedFrom":[makeQuery(id+"F45.boolean.opBoolean","MERGE",FACE,{"derivedFrom":[makeQuery(id+"F41.boolean.opBoolean","MERGE",FACE,{"derivedFrom":[makeQuery(id+"F37.boolean.opBoolean","MERGE",FACE,{"derivedFrom":[makeQuery(id+"F16.boolean.opBoolean","SPLIT",FACE,{"disambiguationData":[TD([makeQuery(id+"F6.boolean.opBoolean","COPY",FACE,{"derivedFrom":makeQuery(id+"F6.opExtrude","CAP_FACE",FACE,{"disambiguationData":[OSD([subQ4])],"isStart":false})})])],"derivedFrom":makeQuery(id+"F8.boolean.opBoolean","MERGE",FACE,{"derivedFrom":[makeQuery(id+"F7.opExtrude","CAP_FACE",FACE,{"disambiguationData":[OSD([subQ4,subQ2])],"isStart":false}),makeQuery(id+"F8.opExtrude","SWEPT_FACE",FACE,{"disambiguationData":[OSD([subQ3,subQ2])]})]})}),makeQuery(id+"F37.opExtrude","SWEPT_FACE",FACE,{"disambiguationData":[OSD([subQ4,subQ3,subQ2,subQ1,subQ0])]})]}),makeQuery(id+"F41.opExtrude","SWEPT_FACE",FACE,{"disambiguationData":[OSD([subQ4,subQ3,subQ2,subQ1,subQ0])]})]}),makeQuery(id+"F45.opExtrude","SWEPT_FACE",FACE,{"disambiguationData":[OSD([subQ4,subQ3,subQ2,subQ1,subQ0])]})]}),makeQuery(id+"F54.opExtrude","SWEPT_FACE",FACE,{"disambiguationData":[OSD([subQ4,subQ3,subQ2,subQ1,subQ0])]})]});}
            var Q1;
            {var subQ0=sQuery(id+"F15.wireOp",EDGE,"E6.right");var subQ1=sQuery(id+"F15.wireOp",EDGE,"E6.bottom");var subQ2=sQuery(id+"F4.wireOp",EDGE,"E1.right");var subQ3=sQuery(id+"F4.wireOp",EDGE,"E1.top");var subQ4=sQuery(id+"F4.wireOp",EDGE,"E1.bottom");var subQ5=sQuery(id+"F15.wireOp",EDGE,"E5.right");var subQ6=sQuery(id+"F15.wireOp",EDGE,"E5.top");Q1=makeQuery(id+"F58.boolean.opBoolean","MERGE",FACE,{"derivedFrom":[makeQuery(id+"F56.boolean.opBoolean","MERGE",FACE,{"derivedFrom":[makeQuery(id+"F52.boolean.opBoolean","MERGE",FACE,{"derivedFrom":[makeQuery(id+"F43.boolean.opBoolean","MERGE",FACE,{"derivedFrom":[makeQuery(id+"F41.boolean.opBoolean","MERGE",FACE,{"derivedFrom":[makeQuery(id+"F35.boolean.opBoolean","MERGE",FACE,{"derivedFrom":[makeQuery(id+"F18.boolean.opBoolean","MERGE",FACE,{"derivedFrom":[makeQuery(id+"F16.boolean.opBoolean","SPLIT",FACE,{"disambiguationData":[TD([makeQuery(id+"F16.opExtrude","SWEPT_FACE",FACE,{"disambiguationData":[OSD([subQ6])]})])],"derivedFrom":makeQuery(id+"F8.boolean.opBoolean","MERGE",FACE,{"derivedFrom":[makeQuery(id+"F7.opExtrude","CAP_FACE",FACE,{"disambiguationData":[OSD([subQ4,subQ2])],"isStart":false}),makeQuery(id+"F8.opExtrude","SWEPT_FACE",FACE,{"disambiguationData":[OSD([subQ3,subQ2])]})]})}),makeQuery(id+"F18.opExtrude","SWEPT_FACE",FACE,{"disambiguationData":[OSD([subQ4,subQ3,subQ2,subQ1,subQ0])]})]}),makeQuery(id+"F35.opExtrude","SWEPT_FACE",FACE,{"disambiguationData":[OSD([subQ4,subQ3,subQ2,subQ6,subQ5])]})]}),makeQuery(id+"F41.opExtrude","SWEPT_FACE",FACE,{"disambiguationData":[OSD([subQ4,subQ3,subQ2,subQ6,subQ5,subQ1,subQ0])]})]}),makeQuery(id+"F43.opExtrude","SWEPT_FACE",FACE,{"disambiguationData":[OSD([subQ4,subQ3,subQ2,subQ1,subQ0])]})]}),makeQuery(id+"F52.opExtrude","SWEPT_FACE",FACE,{"disambiguationData":[OSD([subQ4,subQ3,subQ2,subQ1,subQ0])]})]}),makeQuery(id+"F56.opExtrude","SWEPT_FACE",FACE,{"disambiguationData":[OSD([subQ4,subQ3,subQ2,subQ6,subQ5])]})]}),makeQuery(id+"F58.opExtrude","SWEPT_FACE",FACE,{"disambiguationData":[OSD([subQ4,subQ3,subQ2,subQ1,subQ0])]})]});}
            var Q2;
            {var subQ0=sQuery(id+"F15.wireOp",EDGE,"E6.right");var subQ1=sQuery(id+"F15.wireOp",EDGE,"E6.top");var subQ2=sQuery(id+"F4.wireOp",EDGE,"E1.right");var subQ3=sQuery(id+"F4.wireOp",EDGE,"E1.top");var subQ4=sQuery(id+"F4.wireOp",EDGE,"E1.bottom");Q2=makeQuery(id+"F41.boolean.opBoolean","MERGE",FACE,{"derivedFrom":[makeQuery(id+"F40.boolean.opBoolean","MERGE",FACE,{"derivedFrom":[makeQuery(id+"F38.boolean.opBoolean","MERGE",FACE,{"derivedFrom":[makeQuery(id+"F16.boolean.opBoolean","SPLIT",FACE,{"disambiguationData":[TD([makeQuery(id+"F8.boolean.opBoolean","COPY",FACE,{"derivedFrom":makeQuery(id+"F8.opExtrude","CAP_FACE",FACE,{"disambiguationData":[OSD([subQ3])],"isStart":false})})])],"derivedFrom":makeQuery(id+"F8.boolean.opBoolean","MERGE",FACE,{"derivedFrom":[makeQuery(id+"F7.opExtrude","CAP_FACE",FACE,{"disambiguationData":[OSD([subQ4,subQ2])],"isStart":false}),makeQuery(id+"F8.opExtrude","SWEPT_FACE",FACE,{"disambiguationData":[OSD([subQ3,subQ2])]})]})}),makeQuery(id+"F38.opExtrude","SWEPT_FACE",FACE,{"disambiguationData":[OSD([subQ4,subQ3,subQ2,subQ1,subQ0])]})]}),makeQuery(id+"F40.opExtrude","SWEPT_FACE",FACE,{"disambiguationData":[OSD([subQ4,subQ3,subQ2,subQ1,subQ0])]})]}),makeQuery(id+"F41.opExtrude","SWEPT_FACE",FACE,{"disambiguationData":[OSD([subQ4,subQ3,subQ2,subQ1,subQ0])]})]});}
            extrude(context, id + "F60", {"entities" : qUnion([Q0, Q1, Q2]), "operationType" : NewBodyOperationType.REMOVE, "oppositeDirection" : true, "depth" : 100 * mm, "offsetDistance" : 25 * mm});
        }
        {
            var Q0;
            {var subQ0=sQuery(id+"F15.wireOp",EDGE,"E5.left");var subQ1=sQuery(id+"F15.wireOp",EDGE,"E5.bottom");var subQ2=sQuery(id+"F10.wireOp",EDGE,"E2.right");var subQ6=sQuery(id+"F4.wireOp",EDGE,"E1.bottom");Q0=makeQuery(id+"F54.boolean.opBoolean","MERGE",FACE,{"derivedFrom":[makeQuery(id+"F45.boolean.opBoolean","MERGE",FACE,{"derivedFrom":[makeQuery(id+"F41.boolean.opBoolean","MERGE",FACE,{"derivedFrom":[makeQuery(id+"F37.boolean.opBoolean","MERGE",FACE,{"derivedFrom":[makeQuery(id+"F16.boolean.opBoolean","SPLIT",FACE,{"disambiguationData":[TD([makeQuery(id+"F6.boolean.opBoolean","COPY",FACE,{"derivedFrom":makeQuery(id+"F6.opExtrude","CAP_FACE",FACE,{"disambiguationData":[OSD([subQ6])],"isStart":false})})])],"derivedFrom":makeQuery(id+"F13.boolean.opBoolean","COPY",FACE,{"derivedFrom":makeQuery(id+"F13.opExtrude","CAP_FACE",FACE,{"disambiguationData":[OSD([subQ2])],"isStart":false})})}),makeQuery(id+"F37.opExtrude","SWEPT_FACE",FACE,{"disambiguationData":[OSD([subQ2,subQ1,subQ0])]})]}),makeQuery(id+"F41.opExtrude","SWEPT_FACE",FACE,{"disambiguationData":[OSD([subQ2,subQ1,subQ0])]})]}),makeQuery(id+"F45.opExtrude","SWEPT_FACE",FACE,{"disambiguationData":[OSD([subQ2,subQ1,subQ0])]})]}),makeQuery(id+"F54.opExtrude","SWEPT_FACE",FACE,{"disambiguationData":[OSD([subQ2,subQ1,subQ0])]})]});}
            var Q1;
            {var subQ0=sQuery(id+"F15.wireOp",EDGE,"E6.left");var subQ1=sQuery(id+"F15.wireOp",EDGE,"E6.bottom");var subQ2=sQuery(id+"F10.wireOp",EDGE,"E2.right");var subQ3=sQuery(id+"F15.wireOp",EDGE,"E5.left");var subQ4=sQuery(id+"F15.wireOp",EDGE,"E5.top");Q1=makeQuery(id+"F58.boolean.opBoolean","MERGE",FACE,{"derivedFrom":[makeQuery(id+"F56.boolean.opBoolean","MERGE",FACE,{"derivedFrom":[makeQuery(id+"F52.boolean.opBoolean","MERGE",FACE,{"derivedFrom":[makeQuery(id+"F43.boolean.opBoolean","MERGE",FACE,{"derivedFrom":[makeQuery(id+"F41.boolean.opBoolean","MERGE",FACE,{"derivedFrom":[makeQuery(id+"F35.boolean.opBoolean","MERGE",FACE,{"derivedFrom":[makeQuery(id+"F18.boolean.opBoolean","MERGE",FACE,{"derivedFrom":[makeQuery(id+"F16.boolean.opBoolean","SPLIT",FACE,{"disambiguationData":[TD([makeQuery(id+"F16.opExtrude","SWEPT_FACE",FACE,{"disambiguationData":[OSD([subQ4])]})])],"derivedFrom":makeQuery(id+"F13.boolean.opBoolean","COPY",FACE,{"derivedFrom":makeQuery(id+"F13.opExtrude","CAP_FACE",FACE,{"disambiguationData":[OSD([subQ2])],"isStart":false})})}),makeQuery(id+"F18.opExtrude","SWEPT_FACE",FACE,{"disambiguationData":[OSD([subQ2,subQ1,subQ0])]})]}),makeQuery(id+"F35.opExtrude","SWEPT_FACE",FACE,{"disambiguationData":[OSD([subQ2,subQ4,subQ3])]})]}),makeQuery(id+"F41.opExtrude","SWEPT_FACE",FACE,{"disambiguationData":[OSD([subQ2,subQ4,subQ3,subQ1,subQ0])]})]}),makeQuery(id+"F43.opExtrude","SWEPT_FACE",FACE,{"disambiguationData":[OSD([subQ2,subQ1,subQ0])]})]}),makeQuery(id+"F52.opExtrude","SWEPT_FACE",FACE,{"disambiguationData":[OSD([subQ2,subQ1,subQ0])]})]}),makeQuery(id+"F56.opExtrude","SWEPT_FACE",FACE,{"disambiguationData":[OSD([subQ2,subQ4,subQ3])]})]}),makeQuery(id+"F58.opExtrude","SWEPT_FACE",FACE,{"disambiguationData":[OSD([subQ2,subQ1,subQ0])]})]});}
            var Q2;
            {var subQ0=sQuery(id+"F15.wireOp",EDGE,"E6.left");var subQ1=sQuery(id+"F15.wireOp",EDGE,"E6.top");var subQ2=sQuery(id+"F10.wireOp",EDGE,"E2.right");var subQ3=sQuery(id+"F4.wireOp",EDGE,"E1.top");Q2=makeQuery(id+"F41.boolean.opBoolean","MERGE",FACE,{"derivedFrom":[makeQuery(id+"F40.boolean.opBoolean","MERGE",FACE,{"derivedFrom":[makeQuery(id+"F38.boolean.opBoolean","MERGE",FACE,{"derivedFrom":[makeQuery(id+"F16.boolean.opBoolean","SPLIT",FACE,{"disambiguationData":[TD([makeQuery(id+"F8.boolean.opBoolean","COPY",FACE,{"derivedFrom":makeQuery(id+"F8.opExtrude","CAP_FACE",FACE,{"disambiguationData":[OSD([subQ3])],"isStart":false})})])],"derivedFrom":makeQuery(id+"F13.boolean.opBoolean","COPY",FACE,{"derivedFrom":makeQuery(id+"F13.opExtrude","CAP_FACE",FACE,{"disambiguationData":[OSD([subQ2])],"isStart":false})})}),makeQuery(id+"F38.opExtrude","SWEPT_FACE",FACE,{"disambiguationData":[OSD([subQ2,subQ1,subQ0])]})]}),makeQuery(id+"F40.opExtrude","SWEPT_FACE",FACE,{"disambiguationData":[OSD([subQ2,subQ1,subQ0])]})]}),makeQuery(id+"F41.opExtrude","SWEPT_FACE",FACE,{"disambiguationData":[OSD([subQ2,subQ1,subQ0])]})]});}
            extrude(context, id + "F61", {"entities" : qUnion([Q0, Q1, Q2]), "operationType" : NewBodyOperationType.ADD, "depth" : 50 * mm, "offsetDistance" : 25 * mm});
        }
        {
            var Q0;
            {var subQ0=sQuery(id+"F14.wireOp",EDGE,"E3.right");var subQ1=sQuery(id+"F14.wireOp",EDGE,"E3.bottom");var subQ2=sQuery(id+"F10.wireOp",EDGE,"E2.left");var subQ6=sQuery(id+"F4.wireOp",EDGE,"E1.bottom");Q0=makeQuery(id+"F54.boolean.opBoolean","MERGE",FACE,{"derivedFrom":[makeQuery(id+"F45.boolean.opBoolean","MERGE",FACE,{"derivedFrom":[makeQuery(id+"F41.boolean.opBoolean","MERGE",FACE,{"derivedFrom":[makeQuery(id+"F30.boolean.opBoolean","MERGE",FACE,{"derivedFrom":[makeQuery(id+"F20.boolean.opBoolean","MERGE",FACE,{"derivedFrom":[makeQuery(id+"F16.boolean.opBoolean","SPLIT",FACE,{"disambiguationData":[TD([makeQuery(id+"F6.boolean.opBoolean","COPY",FACE,{"derivedFrom":makeQuery(id+"F6.opExtrude","CAP_FACE",FACE,{"disambiguationData":[OSD([subQ6])],"isStart":false})})])],"derivedFrom":makeQuery(id+"F12.boolean.opBoolean","COPY",FACE,{"derivedFrom":makeQuery(id+"F12.opExtrude","CAP_FACE",FACE,{"disambiguationData":[OSD([subQ2])],"isStart":false})})}),makeQuery(id+"F20.opExtrude","SWEPT_FACE",FACE,{"disambiguationData":[OSD([subQ2,subQ1,subQ0])]})]}),makeQuery(id+"F30.opExtrude","SWEPT_FACE",FACE,{"disambiguationData":[OSD([subQ2,subQ1,subQ0])]})]}),makeQuery(id+"F41.opExtrude","SWEPT_FACE",FACE,{"disambiguationData":[OSD([subQ2,subQ1,subQ0])]})]}),makeQuery(id+"F45.opExtrude","SWEPT_FACE",FACE,{"disambiguationData":[OSD([subQ2,subQ1,subQ0])]})]}),makeQuery(id+"F54.opExtrude","SWEPT_FACE",FACE,{"disambiguationData":[OSD([subQ2,subQ1,subQ0])]})]});}
            var Q1;
            {var subQ0=sQuery(id+"F14.wireOp",EDGE,"E4.right");var subQ1=sQuery(id+"F14.wireOp",EDGE,"E4.bottom");var subQ2=sQuery(id+"F10.wireOp",EDGE,"E2.left");var subQ3=sQuery(id+"F14.wireOp",EDGE,"E3.right");var subQ4=sQuery(id+"F14.wireOp",EDGE,"E3.top");Q1=makeQuery(id+"F58.boolean.opBoolean","MERGE",FACE,{"derivedFrom":[makeQuery(id+"F56.boolean.opBoolean","MERGE",FACE,{"derivedFrom":[makeQuery(id+"F52.boolean.opBoolean","MERGE",FACE,{"derivedFrom":[makeQuery(id+"F43.boolean.opBoolean","MERGE",FACE,{"derivedFrom":[makeQuery(id+"F41.boolean.opBoolean","MERGE",FACE,{"derivedFrom":[makeQuery(id+"F34.boolean.opBoolean","MERGE",FACE,{"derivedFrom":[makeQuery(id+"F32.boolean.opBoolean","MERGE",FACE,{"derivedFrom":[makeQuery(id+"F26.boolean.opBoolean","MERGE",FACE,{"derivedFrom":[makeQuery(id+"F24.boolean.opBoolean","MERGE",FACE,{"derivedFrom":[makeQuery(id+"F18.boolean.opBoolean","MERGE",FACE,{"derivedFrom":[makeQuery(id+"F16.boolean.opBoolean","SPLIT",FACE,{"disambiguationData":[TD([makeQuery(id+"F16.opExtrude","SWEPT_FACE",FACE,{"disambiguationData":[OSD([subQ4])]})])],"derivedFrom":makeQuery(id+"F12.boolean.opBoolean","COPY",FACE,{"derivedFrom":makeQuery(id+"F12.opExtrude","CAP_FACE",FACE,{"disambiguationData":[OSD([subQ2])],"isStart":false})})}),makeQuery(id+"F18.opExtrude","SWEPT_FACE",FACE,{"disambiguationData":[OSD([subQ2,subQ1,subQ0])]})]}),makeQuery(id+"F24.opExtrude","SWEPT_FACE",FACE,{"disambiguationData":[OSD([subQ2,subQ4,subQ3])]})]}),makeQuery(id+"F26.opExtrude","SWEPT_FACE",FACE,{"disambiguationData":[OSD([subQ2,subQ4,subQ3])]})]}),makeQuery(id+"F32.opExtrude","SWEPT_FACE",FACE,{"disambiguationData":[OSD([subQ2,subQ4,subQ3])]})]}),makeQuery(id+"F34.opExtrude","SWEPT_FACE",FACE,{"disambiguationData":[OSD([subQ2,subQ1,subQ0])]})]}),makeQuery(id+"F41.opExtrude","SWEPT_FACE",FACE,{"disambiguationData":[OSD([subQ2,subQ4,subQ3,subQ1,subQ0])]})]}),makeQuery(id+"F43.opExtrude","SWEPT_FACE",FACE,{"disambiguationData":[OSD([subQ2,subQ1,subQ0])]})]}),makeQuery(id+"F52.opExtrude","SWEPT_FACE",FACE,{"disambiguationData":[OSD([subQ2,subQ1,subQ0])]})]}),makeQuery(id+"F56.opExtrude","SWEPT_FACE",FACE,{"disambiguationData":[OSD([subQ2,subQ4,subQ3])]})]}),makeQuery(id+"F58.opExtrude","SWEPT_FACE",FACE,{"disambiguationData":[OSD([subQ2,subQ1,subQ0])]})]});}
            var Q2;
            {var subQ0=sQuery(id+"F14.wireOp",EDGE,"E4.right");var subQ1=sQuery(id+"F14.wireOp",EDGE,"E4.top");var subQ2=sQuery(id+"F10.wireOp",EDGE,"E2.left");var subQ3=sQuery(id+"F4.wireOp",EDGE,"E1.top");Q2=makeQuery(id+"F41.boolean.opBoolean","MERGE",FACE,{"derivedFrom":[makeQuery(id+"F28.boolean.opBoolean","MERGE",FACE,{"derivedFrom":[makeQuery(id+"F22.boolean.opBoolean","MERGE",FACE,{"derivedFrom":[makeQuery(id+"F16.boolean.opBoolean","SPLIT",FACE,{"disambiguationData":[TD([makeQuery(id+"F8.boolean.opBoolean","COPY",FACE,{"derivedFrom":makeQuery(id+"F8.opExtrude","CAP_FACE",FACE,{"disambiguationData":[OSD([subQ3])],"isStart":false})})])],"derivedFrom":makeQuery(id+"F12.boolean.opBoolean","COPY",FACE,{"derivedFrom":makeQuery(id+"F12.opExtrude","CAP_FACE",FACE,{"disambiguationData":[OSD([subQ2])],"isStart":false})})}),makeQuery(id+"F22.opExtrude","SWEPT_FACE",FACE,{"disambiguationData":[OSD([subQ2,subQ1,subQ0])]})]}),makeQuery(id+"F28.opExtrude","SWEPT_FACE",FACE,{"disambiguationData":[OSD([subQ2,subQ1,subQ0])]})]}),makeQuery(id+"F41.opExtrude","SWEPT_FACE",FACE,{"disambiguationData":[OSD([subQ2,subQ1,subQ0])]})]});}
            extrude(context, id + "F62", {"entities" : qUnion([Q0, Q1, Q2]), "operationType" : NewBodyOperationType.REMOVE, "oppositeDirection" : true, "depth" : 50 * mm, "offsetDistance" : 25 * mm});
        }
        {
            var Q0;
            {var subQ0=sQuery(id+"F15.wireOp",EDGE,"E6.left");var subQ1=sQuery(id+"F15.wireOp",EDGE,"E6.bottom");var subQ2=sQuery(id+"F10.wireOp",EDGE,"E2.right");var subQ3=makeQuery(id+"F16.opExtrude","CAP_VERTEX",VERTEX,{"disambiguationData":[OSD([subQ2,subQ1,subQ0])],"isStart":false});var subQ4=makeQuery(id+"F39.opExtrude","CAP_VERTEX",VERTEX,{"disambiguationData":[OSD([subQ2,subQ1,subQ0]),TDD([makeQuery(id+"F18.boolean.opBoolean","COPY",VERTEX,{"derivedFrom":makeQuery(id+"F18.opExtrude","CAP_VERTEX",VERTEX,{"disambiguationData":[OSD([subQ2,subQ1,subQ0]),TDD([subQ3])],"isStart":false})})])],"isStart":false});var subQ5=makeQuery(id+"F43.boolean.opBoolean","COPY",VERTEX,{"derivedFrom":makeQuery(id+"F43.opExtrude","CAP_VERTEX",VERTEX,{"disambiguationData":[OSD([subQ2,subQ1,subQ0]),TDD([subQ4])],"isStart":false})});var subQ6=sQuery(id+"F15.wireOp",EDGE,"E5.left");var subQ7=sQuery(id+"F15.wireOp",EDGE,"E5.top");var subQ8=makeQuery(id+"F16.opExtrude","CAP_VERTEX",VERTEX,{"disambiguationData":[OSD([subQ2,subQ7,subQ6])],"isStart":false});var subQ9=sQuery(id+"F15.wireOp",EDGE,"E5.bottom");var subQ10=makeQuery(id+"F16.opExtrude","CAP_FACE",FACE,{"disambiguationData":[OSD([subQ9,subQ7,subQ6,sQuery(id+"F15.wireOp",EDGE,"E5.right")])],"isStart":false});var subQ11=sQuery(id+"F14.wireOp",EDGE,"E4.top");var subQ12=sQuery(id+"F14.wireOp",EDGE,"E4.bottom");var subQ13=makeQuery(id+"F16.opExtrude","CAP_FACE",FACE,{"disambiguationData":[OSD([subQ12,subQ11,sQuery(id+"F14.wireOp",EDGE,"E4.left"),sQuery(id+"F14.wireOp",EDGE,"E4.right")])],"isStart":false});var subQ14=sQuery(id+"F14.wireOp",EDGE,"E3.top");var subQ15=sQuery(id+"F14.wireOp",EDGE,"E3.bottom");var subQ16=makeQuery(id+"F16.opExtrude","CAP_FACE",FACE,{"disambiguationData":[OSD([subQ15,subQ14,sQuery(id+"F14.wireOp",EDGE,"E3.left"),sQuery(id+"F14.wireOp",EDGE,"E3.right")])],"isStart":false});var subQ18=sQuery(id+"F10.wireOp",EDGE,"E2.left");var subQ19=sQuery(id+"F10.wireOp",EDGE,"E2.top");var subQ20=sQuery(id+"F10.wireOp",EDGE,"E2.bottom");var subQ21=makeQuery(id+"F11.opExtrude","CAP_FACE",FACE,{"disambiguationData":[OSD([subQ20,subQ19,subQ18,subQ2])],"isStart":false});var subQ22=sQuery(id+"F0.wireOp",EDGE,"E0.left");var subQ23=makeQuery(id+"F1.opExtrude","CAP_EDGE",EDGE,{"disambiguationData":[OSD([subQ22])],"isStart":false});var subQ24=makeQuery(id+"F2.opExtrude","SWEPT_FACE",FACE,{"disambiguationData":[OSD([subQ22]),TDD([subQ23])]});var subQ25=sQuery(id+"F4.wireOp",EDGE,"E1.left");var subQ26=sQuery(id+"F4.wireOp",EDGE,"E1.top");var subQ27=sQuery(id+"F4.wireOp",EDGE,"E1.bottom");var subQ28=makeQuery(id+"F9.opExtrude","SWEPT_FACE",FACE,{"disambiguationData":[OSD([subQ27,subQ26,subQ25]),TDD([makeQuery(id+"F8.boolean.opBoolean","MERGE",EDGE,{"derivedFrom":[makeQuery(id+"F6.boolean.opBoolean","MERGE",EDGE,{"derivedFrom":[makeQuery(id+"F5.boolean.opBoolean","COPY",EDGE,{"derivedFrom":makeQuery(id+"F5.opExtrude","CAP_EDGE",EDGE,{"disambiguationData":[OSD([subQ25])],"isStart":true})}),makeQuery(id+"F6.opExtrude","SWEPT_EDGE",EDGE,{"disambiguationData":[OSD([subQ27,subQ25]),TDD([makeQuery(id+"F5.boolean.opBoolean","COPY",VERTEX,{"derivedFrom":makeQuery(id+"F5.opExtrude","CAP_VERTEX",VERTEX,{"disambiguationData":[OSD([subQ27,subQ25])],"isStart":true})})])]})]}),makeQuery(id+"F8.opExtrude","SWEPT_EDGE",EDGE,{"disambiguationData":[OSD([subQ26,subQ25]),TDD([makeQuery(id+"F5.boolean.opBoolean","COPY",VERTEX,{"derivedFrom":makeQuery(id+"F5.opExtrude","CAP_VERTEX",VERTEX,{"disambiguationData":[OSD([subQ26,subQ25])],"isStart":true})})])]})]})])]});var subQ29=sQuery(id+"F0.wireOp",EDGE,"E0.bottom");var subQ30=makeQuery(id+"F1.opExtrude","CAP_FACE",FACE,{"disambiguationData":[OSD([subQ29,sQuery(id+"F0.wireOp",EDGE,"E0.top"),subQ22,sQuery(id+"F0.wireOp",EDGE,"E0.right")])],"isStart":false});var subQ31=sQuery(id+"F4.wireOp",EDGE,"E1.right");var subQ32=makeQuery(id+"F7.opExtrude","SWEPT_FACE",FACE,{"disambiguationData":[OSD([subQ27,subQ31]),TDD([makeQuery(id+"F6.boolean.opBoolean","MERGE",EDGE,{"derivedFrom":[makeQuery(id+"F5.boolean.opBoolean","COPY",EDGE,{"derivedFrom":makeQuery(id+"F5.opExtrude","CAP_EDGE",EDGE,{"disambiguationData":[OSD([subQ31])],"isStart":true})}),makeQuery(id+"F6.opExtrude","SWEPT_EDGE",EDGE,{"disambiguationData":[OSD([subQ27,subQ31]),TDD([makeQuery(id+"F5.boolean.opBoolean","COPY",VERTEX,{"derivedFrom":makeQuery(id+"F5.opExtrude","CAP_VERTEX",VERTEX,{"disambiguationData":[OSD([subQ27,subQ31])],"isStart":true})})])]})]})])]});var subQ33=makeQuery(id+"F1.opExtrude","CAP_VERTEX",VERTEX,{"disambiguationData":[OSD([subQ29,subQ22])],"isStart":false});var subQ34=makeQuery(id+"F3.opExtrude","SWEPT_FACE",FACE,{"disambiguationData":[OSD([subQ29,subQ22]),TDD([makeQuery(id+"F2.boolean.opBoolean","MERGE",EDGE,{"derivedFrom":[makeQuery(id+"F1.opExtrude","CAP_EDGE",EDGE,{"disambiguationData":[OSD([subQ29])],"isStart":false}),makeQuery(id+"F2.opExtrude","SWEPT_EDGE",EDGE,{"disambiguationData":[OSD([subQ29,subQ22]),TDD([subQ33])]})]})])]});var subQ35=sQuery(id+"F15.wireOp",EDGE,"E6.top");var subQ36=makeQuery(id+"F16.opExtrude","CAP_FACE",FACE,{"disambiguationData":[OSD([subQ1,subQ35,subQ0,sQuery(id+"F15.wireOp",EDGE,"E6.right")])],"isStart":false});var subQ37=makeQuery(id+"F13.boolean.opBoolean","COPY",EDGE,{"derivedFrom":makeQuery(id+"F13.opExtrude","CAP_EDGE",EDGE,{"disambiguationData":[OSD([subQ2]),TDD([makeQuery(id+"F11.opExtrude","CAP_EDGE",EDGE,{"disambiguationData":[OSD([subQ2])],"isStart":false})])],"isStart":false})});var subQ38=makeQuery(id+"F17.opExtrude","CAP_VERTEX",VERTEX,{"disambiguationData":[OSD([subQ2,subQ35,subQ0]),TDD([makeQuery(id+"F16.opExtrude","CAP_VERTEX",VERTEX,{"disambiguationData":[OSD([subQ2,subQ35,subQ0])],"isStart":false})])],"isStart":false});var subQ39=makeQuery(id+"F16.opExtrude","CAP_VERTEX",VERTEX,{"disambiguationData":[OSD([subQ2,subQ9,subQ6])],"isStart":false});var subQ40=makeQuery(id+"F37.boolean.opBoolean","COPY",VERTEX,{"derivedFrom":makeQuery(id+"F37.opExtrude","CAP_VERTEX",VERTEX,{"disambiguationData":[OSD([subQ2,subQ9,subQ6]),TDD([subQ39])],"isStart":false})});var subQ41=makeQuery(id+"F6.boolean.opBoolean","COPY",FACE,{"derivedFrom":makeQuery(id+"F6.opExtrude","CAP_FACE",FACE,{"disambiguationData":[OSD([subQ27])],"isStart":false})});var subQ42=makeQuery(id+"F16.opExtrude","CAP_EDGE",EDGE,{"disambiguationData":[OSD([subQ35])],"isStart":false});var subQ43=makeQuery(id+"F40.boolean.opBoolean","COPY",EDGE,{"derivedFrom":makeQuery(id+"F40.opExtrude","CAP_EDGE",EDGE,{"disambiguationData":[OSD([subQ35]),TDD([makeQuery(id+"F38.boolean.opBoolean","COPY",EDGE,{"derivedFrom":makeQuery(id+"F38.opExtrude","CAP_EDGE",EDGE,{"disambiguationData":[OSD([subQ35]),TDD([makeQuery(id+"F17.opExtrude","CAP_EDGE",EDGE,{"disambiguationData":[OSD([subQ35]),TDD([subQ42])],"isStart":false})])],"isStart":false})})])],"isStart":false})});var subQ44=makeQuery(id+"F42.opExtrude","CAP_EDGE",EDGE,{"disambiguationData":[OSD([subQ35]),TDD([subQ43])],"isStart":false});var subQ45=makeQuery(id+"F16.opExtrude","CAP_EDGE",EDGE,{"disambiguationData":[OSD([subQ11])],"isStart":false});var subQ46=makeQuery(id+"F22.boolean.opBoolean","COPY",EDGE,{"derivedFrom":makeQuery(id+"F22.opExtrude","CAP_EDGE",EDGE,{"disambiguationData":[OSD([subQ11]),TDD([makeQuery(id+"F17.opExtrude","CAP_EDGE",EDGE,{"disambiguationData":[OSD([subQ11]),TDD([subQ45])],"isStart":false})])],"isStart":false})});var subQ47=makeQuery(id+"F28.boolean.opBoolean","COPY",EDGE,{"derivedFrom":makeQuery(id+"F28.opExtrude","CAP_EDGE",EDGE,{"disambiguationData":[OSD([subQ11]),TDD([makeQuery(id+"F27.opExtrude","CAP_EDGE",EDGE,{"disambiguationData":[OSD([subQ11]),TDD([subQ46])],"isStart":false})])],"isStart":false})});var subQ48=makeQuery(id+"F33.opExtrude","CAP_EDGE",EDGE,{"disambiguationData":[OSD([subQ11]),TDD([subQ47])],"isStart":false});var subQ49=makeQuery(id+"F42.opExtrude","CAP_EDGE",EDGE,{"disambiguationData":[OSD([subQ11]),TDD([subQ48])],"isStart":false});var subQ50=makeQuery(id+"F20.boolean.opBoolean","COPY",EDGE,{"derivedFrom":makeQuery(id+"F20.opExtrude","CAP_EDGE",EDGE,{"disambiguationData":[OSD([subQ15]),TDD([makeQuery(id+"F16.opExtrude","CAP_EDGE",EDGE,{"disambiguationData":[OSD([subQ15])],"isStart":false})])],"isStart":false})});var subQ51=makeQuery(id+"F23.opExtrude","CAP_EDGE",EDGE,{"disambiguationData":[OSD([subQ15]),TDD([subQ50])],"isStart":false});var subQ52=makeQuery(id+"F30.boolean.opBoolean","COPY",EDGE,{"derivedFrom":makeQuery(id+"F30.opExtrude","CAP_EDGE",EDGE,{"disambiguationData":[OSD([subQ15]),TDD([makeQuery(id+"F25.opExtrude","CAP_EDGE",EDGE,{"disambiguationData":[OSD([subQ15]),TDD([subQ51])],"isStart":false})])],"isStart":false})});var subQ53=makeQuery(id+"F35.boolean.opBoolean","COPY",EDGE,{"derivedFrom":makeQuery(id+"F35.opExtrude","CAP_EDGE",EDGE,{"disambiguationData":[OSD([subQ7]),TDD([makeQuery(id+"F16.opExtrude","CAP_EDGE",EDGE,{"disambiguationData":[OSD([subQ7])],"isStart":false})])],"isStart":false})});var subQ54=makeQuery(id+"F36.opExtrude","CAP_EDGE",EDGE,{"disambiguationData":[OSD([subQ7]),TDD([subQ53])],"isStart":false});var subQ55=makeQuery(id+"F16.opExtrude","CAP_EDGE",EDGE,{"disambiguationData":[OSD([subQ14])],"isStart":false});var subQ56=makeQuery(id+"F26.boolean.opBoolean","COPY",EDGE,{"derivedFrom":makeQuery(id+"F26.opExtrude","CAP_EDGE",EDGE,{"disambiguationData":[OSD([subQ14]),TDD([makeQuery(id+"F24.boolean.opBoolean","COPY",EDGE,{"derivedFrom":makeQuery(id+"F24.opExtrude","CAP_EDGE",EDGE,{"disambiguationData":[OSD([subQ14]),TDD([makeQuery(id+"F19.opExtrude","CAP_EDGE",EDGE,{"disambiguationData":[OSD([subQ14]),TDD([subQ55])],"isStart":false})])],"isStart":false})})])],"isStart":false})});var subQ57=makeQuery(id+"F32.boolean.opBoolean","COPY",EDGE,{"derivedFrom":makeQuery(id+"F32.opExtrude","CAP_EDGE",EDGE,{"disambiguationData":[OSD([subQ14]),TDD([makeQuery(id+"F29.opExtrude","CAP_EDGE",EDGE,{"disambiguationData":[OSD([subQ14]),TDD([subQ56])],"isStart":false})])],"isStart":false})});var subQ58=makeQuery(id+"F6.boolean.opBoolean","COPY",EDGE,{"derivedFrom":makeQuery(id+"F6.opExtrude","CAP_EDGE",EDGE,{"disambiguationData":[OSD([subQ27]),TDD([makeQuery(id+"F5.boolean.opBoolean","COPY",EDGE,{"derivedFrom":makeQuery(id+"F5.opExtrude","CAP_EDGE",EDGE,{"disambiguationData":[OSD([subQ27])],"isStart":true})})])],"isStart":false})});var subQ59=makeQuery(id+"F13.boolean.opBoolean","MERGE",EDGE,{"derivedFrom":[makeQuery(id+"F11.boolean.opBoolean","SPLIT",EDGE,{"disambiguationData":[TD([makeQuery(id+"F11.opExtrude","SWEPT_FACE",FACE,{"disambiguationData":[OSD([subQ2])]})])],"derivedFrom":subQ58}),makeQuery(id+"F13.opExtrude","SWEPT_EDGE",EDGE,{"disambiguationData":[OSD([subQ27,subQ20,subQ2]),TDD([makeQuery(id+"F11.opExtrude","CAP_VERTEX",VERTEX,{"disambiguationData":[OSD([subQ27,subQ20,subQ2])],"isStart":false})])]})]});var subQ60=makeQuery(id+"F12.boolean.opBoolean","MERGE",EDGE,{"derivedFrom":[makeQuery(id+"F11.boolean.opBoolean","SPLIT",EDGE,{"disambiguationData":[TD([makeQuery(id+"F11.opExtrude","SWEPT_FACE",FACE,{"disambiguationData":[OSD([subQ18])]})])],"derivedFrom":subQ58}),makeQuery(id+"F12.opExtrude","SWEPT_EDGE",EDGE,{"disambiguationData":[OSD([subQ27,subQ20,subQ18]),TDD([makeQuery(id+"F11.opExtrude","CAP_VERTEX",VERTEX,{"disambiguationData":[OSD([subQ27,subQ20,subQ18])],"isStart":false})])]})]});Q0=makeQuery(id+"F61.boolean.opBoolean","MERGE",FACE,{"derivedFrom":[makeQuery(id+"F59.boolean.opBoolean","MERGE",FACE,{"derivedFrom":[makeQuery(id+"F57.boolean.opBoolean","MERGE",FACE,{"derivedFrom":[makeQuery(id+"F55.boolean.opBoolean","MERGE",FACE,{"derivedFrom":[makeQuery(id+"F53.boolean.opBoolean","MERGE",FACE,{"derivedFrom":[makeQuery(id+"F51.boolean.opBoolean","MERGE",FACE,{"derivedFrom":[makeQuery(id+"F50.boolean.opBoolean","MERGE",FACE,{"derivedFrom":[makeQuery(id+"F48.boolean.opBoolean","MERGE",FACE,{"derivedFrom":[makeQuery(id+"F46.boolean.opBoolean","MERGE",FACE,{"derivedFrom":[makeQuery(id+"F44.boolean.opBoolean","MERGE",FACE,{"derivedFrom":[makeQuery(id+"F42.boolean.opBoolean","MERGE",FACE,{"derivedFrom":[makeQuery(id+"F39.boolean.opBoolean","MERGE",FACE,{"derivedFrom":[makeQuery(id+"F36.boolean.opBoolean","MERGE",FACE,{"derivedFrom":[makeQuery(id+"F33.boolean.opBoolean","MERGE",FACE,{"derivedFrom":[makeQuery(id+"F31.boolean.opBoolean","MERGE",FACE,{"derivedFrom":[makeQuery(id+"F29.boolean.opBoolean","MERGE",FACE,{"derivedFrom":[makeQuery(id+"F27.boolean.opBoolean","MERGE",FACE,{"derivedFrom":[makeQuery(id+"F25.boolean.opBoolean","MERGE",FACE,{"derivedFrom":[makeQuery(id+"F23.boolean.opBoolean","MERGE",FACE,{"derivedFrom":[makeQuery(id+"F21.boolean.opBoolean","MERGE",FACE,{"derivedFrom":[makeQuery(id+"F19.boolean.opBoolean","MERGE",FACE,{"derivedFrom":[makeQuery(id+"F17.boolean.opBoolean","MERGE",FACE,{"derivedFrom":[makeQuery(id+"F16.boolean.opBoolean","MERGE",FACE,{"derivedFrom":[makeQuery(id+"F11.boolean.opBoolean","MERGE",FACE,{"derivedFrom":[makeQuery(id+"F9.boolean.opBoolean","MERGE",FACE,{"derivedFrom":[makeQuery(id+"F7.boolean.opBoolean","MERGE",FACE,{"derivedFrom":[makeQuery(id+"F3.boolean.opBoolean","MERGE",FACE,{"derivedFrom":[makeQuery(id+"F2.boolean.opBoolean","MERGE",FACE,{"derivedFrom":[subQ30,subQ24]}),subQ34]}),subQ32]}),subQ28]}),subQ21]}),subQ16,subQ13,subQ10,subQ36]}),makeQuery(id+"F17.opExtrude","SWEPT_FACE",FACE,{"disambiguationData":[OSD([subQ11]),TDD([subQ45])]}),makeQuery(id+"F17.opExtrude","SWEPT_FACE",FACE,{"disambiguationData":[OSD([subQ35]),TDD([subQ42])]})]}),makeQuery(id+"F19.opExtrude","SWEPT_FACE",FACE,{"disambiguationData":[OSD([subQ14]),TDD([subQ55])]})]}),makeQuery(id+"F21.opExtrude","SWEPT_FACE",FACE,{"disambiguationData":[OSD([subQ12]),TDD([makeQuery(id+"F18.boolean.opBoolean","COPY",EDGE,{"derivedFrom":makeQuery(id+"F18.opExtrude","CAP_EDGE",EDGE,{"disambiguationData":[OSD([subQ12]),TDD([makeQuery(id+"F16.opExtrude","CAP_EDGE",EDGE,{"disambiguationData":[OSD([subQ12])],"isStart":false})])],"isStart":false})})])]})]}),makeQuery(id+"F23.opExtrude","SWEPT_FACE",FACE,{"disambiguationData":[OSD([subQ15]),TDD([subQ50])]})]}),makeQuery(id+"F25.opExtrude","SWEPT_FACE",FACE,{"disambiguationData":[OSD([subQ15]),TDD([subQ51])]})]}),makeQuery(id+"F27.opExtrude","SWEPT_FACE",FACE,{"disambiguationData":[OSD([subQ11]),TDD([subQ46])]})]}),makeQuery(id+"F29.opExtrude","SWEPT_FACE",FACE,{"disambiguationData":[OSD([subQ14]),TDD([subQ56])]})]}),makeQuery(id+"F31.opExtrude","SWEPT_FACE",FACE,{"disambiguationData":[OSD([subQ15]),TDD([subQ52])]})]}),makeQuery(id+"F33.opExtrude","SWEPT_FACE",FACE,{"disambiguationData":[OSD([subQ11]),TDD([subQ47])]})]}),makeQuery(id+"F36.opExtrude","SWEPT_FACE",FACE,{"disambiguationData":[OSD([subQ7]),TDD([subQ53])]})]}),makeQuery(id+"F39.opExtrude","SWEPT_FACE",FACE,{"disambiguationData":[OSD([subQ1]),TDD([makeQuery(id+"F18.boolean.opBoolean","COPY",EDGE,{"derivedFrom":makeQuery(id+"F18.opExtrude","CAP_EDGE",EDGE,{"disambiguationData":[OSD([subQ1]),TDD([makeQuery(id+"F16.opExtrude","CAP_EDGE",EDGE,{"disambiguationData":[OSD([subQ1])],"isStart":false})])],"isStart":false})})])]})]}),makeQuery(id+"F42.opExtrude","SWEPT_FACE",FACE,{"disambiguationData":[OSD([subQ11]),TDD([subQ48])]}),makeQuery(id+"F42.opExtrude","SWEPT_FACE",FACE,{"disambiguationData":[OSD([subQ35]),TDD([subQ43])]})]}),makeQuery(id+"F44.opExtrude","SWEPT_FACE",FACE,{"disambiguationData":[OSD([subQ14]),TDD([subQ57])]}),makeQuery(id+"F44.opExtrude","SWEPT_FACE",FACE,{"disambiguationData":[OSD([subQ7]),TDD([subQ54])]})]}),makeQuery(id+"F46.opExtrude","SWEPT_FACE",FACE,{"disambiguationData":[OSD([subQ27,subQ20,subQ18]),TDD([subQ60])]}),makeQuery(id+"F46.opExtrude","SWEPT_FACE",FACE,{"disambiguationData":[OSD([subQ27,subQ20,subQ2]),TDD([subQ59])]})]}),makeQuery(id+"F48.opExtrude","SWEPT_FACE",FACE,{"disambiguationData":[OSD([subQ27,subQ20,subQ18]),TDD([makeQuery(id+"F46.opExtrude","CAP_EDGE",EDGE,{"disambiguationData":[OSD([subQ27,subQ20,subQ18]),TDD([subQ60])],"isStart":false})])]}),makeQuery(id+"F48.opExtrude","SWEPT_FACE",FACE,{"disambiguationData":[OSD([subQ27,subQ20,subQ2]),TDD([makeQuery(id+"F46.opExtrude","CAP_EDGE",EDGE,{"disambiguationData":[OSD([subQ27,subQ20,subQ2]),TDD([subQ59])],"isStart":false})])]})]}),makeQuery(id+"F50.opExtrude","SWEPT_FACE",FACE,{"disambiguationData":[OSD([subQ11]),TDD([subQ49])]})]}),makeQuery(id+"F51.opExtrude","SWEPT_FACE",FACE,{"disambiguationData":[OSD([subQ35]),TDD([subQ44])]})]}),makeQuery(id+"F53.opExtrude","SWEPT_FACE",FACE,{"disambiguationData":[OSD([subQ14]),TDD([makeQuery(id+"F44.opExtrude","CAP_EDGE",EDGE,{"disambiguationData":[OSD([subQ14]),TDD([subQ57])],"isStart":false})])]}),makeQuery(id+"F53.opExtrude","SWEPT_FACE",FACE,{"disambiguationData":[OSD([subQ7]),TDD([makeQuery(id+"F44.opExtrude","CAP_EDGE",EDGE,{"disambiguationData":[OSD([subQ7]),TDD([subQ54])],"isStart":false})])]})]}),makeQuery(id+"F55.opExtrude","SWEPT_FACE",FACE,{"disambiguationData":[OSD([subQ15]),TDD([makeQuery(id+"F54.boolean.opBoolean","COPY",EDGE,{"derivedFrom":makeQuery(id+"F54.opExtrude","CAP_EDGE",EDGE,{"disambiguationData":[OSD([subQ15]),TDD([makeQuery(id+"F45.boolean.opBoolean","COPY",EDGE,{"derivedFrom":makeQuery(id+"F45.opExtrude","CAP_EDGE",EDGE,{"disambiguationData":[OSD([subQ15]),TDD([makeQuery(id+"F31.opExtrude","CAP_EDGE",EDGE,{"disambiguationData":[OSD([subQ15]),TDD([subQ52])],"isStart":false})])],"isStart":false})})])],"isStart":false})})])]}),makeQuery(id+"F55.opExtrude","SWEPT_FACE",FACE,{"disambiguationData":[OSD([subQ9]),TDD([makeQuery(id+"F54.boolean.opBoolean","COPY",EDGE,{"derivedFrom":makeQuery(id+"F54.opExtrude","CAP_EDGE",EDGE,{"disambiguationData":[OSD([subQ9]),TDD([makeQuery(id+"F45.boolean.opBoolean","COPY",EDGE,{"derivedFrom":makeQuery(id+"F45.opExtrude","CAP_EDGE",EDGE,{"disambiguationData":[OSD([subQ9]),TDD([makeQuery(id+"F37.boolean.opBoolean","COPY",EDGE,{"derivedFrom":makeQuery(id+"F37.opExtrude","CAP_EDGE",EDGE,{"disambiguationData":[OSD([subQ9]),TDD([makeQuery(id+"F16.opExtrude","CAP_EDGE",EDGE,{"disambiguationData":[OSD([subQ9])],"isStart":false})])],"isStart":false})})])],"isStart":false})})])],"isStart":false})})])]})]}),makeQuery(id+"F57.opExtrude","SWEPT_FACE",FACE,{"disambiguationData":[OSD([subQ11]),TDD([makeQuery(id+"F50.opExtrude","CAP_EDGE",EDGE,{"disambiguationData":[OSD([subQ11]),TDD([subQ49])],"isStart":false})])]}),makeQuery(id+"F57.opExtrude","SWEPT_FACE",FACE,{"disambiguationData":[OSD([subQ35]),TDD([makeQuery(id+"F51.opExtrude","CAP_EDGE",EDGE,{"disambiguationData":[OSD([subQ35]),TDD([subQ44])],"isStart":false})])]})]}),makeQuery(id+"F59.opExtrude","SWEPT_FACE",FACE,{"disambiguationData":[OSD([subQ29,subQ22]),TDD([makeQuery(id+"F3.boolean.opBoolean","MERGE",EDGE,{"derivedFrom":[makeQuery(id+"F2.opExtrude","CAP_EDGE",EDGE,{"disambiguationData":[OSD([subQ22]),TDD([subQ23])],"isStart":false}),makeQuery(id+"F3.opExtrude","SWEPT_EDGE",EDGE,{"disambiguationData":[OSD([subQ29,subQ22]),TDD([makeQuery(id+"F2.opExtrude","CAP_VERTEX",VERTEX,{"disambiguationData":[OSD([subQ29,subQ22]),TDD([subQ33])],"isStart":false})])]})]})])]})]}),makeQuery(id+"F61.opExtrude","SWEPT_FACE",FACE,{"disambiguationData":[OSD([subQ2,subQ9,subQ6]),TDD([makeQuery(id+"F54.boolean.opBoolean","MERGE",EDGE,{"derivedFrom":[makeQuery(id+"F45.boolean.opBoolean","MERGE",EDGE,{"derivedFrom":[makeQuery(id+"F37.boolean.opBoolean","MERGE",EDGE,{"derivedFrom":[makeQuery(id+"F16.boolean.opBoolean","SPLIT",EDGE,{"disambiguationData":[TD([subQ41])],"derivedFrom":subQ37}),makeQuery(id+"F37.opExtrude","SWEPT_EDGE",EDGE,{"disambiguationData":[OSD([subQ2,subQ9,subQ6]),TDD([subQ39])]})]}),makeQuery(id+"F45.opExtrude","SWEPT_EDGE",EDGE,{"disambiguationData":[OSD([subQ2,subQ9,subQ6]),TDD([subQ40])]})]}),makeQuery(id+"F54.opExtrude","SWEPT_EDGE",EDGE,{"disambiguationData":[OSD([subQ2,subQ9,subQ6]),TDD([makeQuery(id+"F45.boolean.opBoolean","COPY",VERTEX,{"derivedFrom":makeQuery(id+"F45.opExtrude","CAP_VERTEX",VERTEX,{"disambiguationData":[OSD([subQ2,subQ9,subQ6]),TDD([subQ40])],"isStart":false})})])]})]})])]}),makeQuery(id+"F61.opExtrude","SWEPT_FACE",FACE,{"disambiguationData":[OSD([subQ2,subQ35,subQ0]),TDD([makeQuery(id+"F40.boolean.opBoolean","MERGE",EDGE,{"derivedFrom":[makeQuery(id+"F38.boolean.opBoolean","MERGE",EDGE,{"derivedFrom":[makeQuery(id+"F16.boolean.opBoolean","SPLIT",EDGE,{"disambiguationData":[TD([makeQuery(id+"F8.boolean.opBoolean","COPY",FACE,{"derivedFrom":makeQuery(id+"F8.opExtrude","CAP_FACE",FACE,{"disambiguationData":[OSD([subQ26])],"isStart":false})})])],"derivedFrom":subQ37}),makeQuery(id+"F38.opExtrude","SWEPT_EDGE",EDGE,{"disambiguationData":[OSD([subQ2,subQ35,subQ0]),TDD([subQ38])]})]}),makeQuery(id+"F40.opExtrude","SWEPT_EDGE",EDGE,{"disambiguationData":[OSD([subQ2,subQ35,subQ0]),TDD([makeQuery(id+"F38.boolean.opBoolean","COPY",VERTEX,{"derivedFrom":makeQuery(id+"F38.opExtrude","CAP_VERTEX",VERTEX,{"disambiguationData":[OSD([subQ2,subQ35,subQ0]),TDD([subQ38])],"isStart":false})})])]})]})])]}),makeQuery(id+"F61.opExtrude","SWEPT_FACE",FACE,{"disambiguationData":[OSD([subQ2,subQ7,subQ6,subQ1,subQ0]),TDD([makeQuery(id+"F58.boolean.opBoolean","MERGE",EDGE,{"derivedFrom":[makeQuery(id+"F56.boolean.opBoolean","MERGE",EDGE,{"derivedFrom":[makeQuery(id+"F52.boolean.opBoolean","MERGE",EDGE,{"derivedFrom":[makeQuery(id+"F43.boolean.opBoolean","MERGE",EDGE,{"derivedFrom":[makeQuery(id+"F35.boolean.opBoolean","MERGE",EDGE,{"derivedFrom":[makeQuery(id+"F18.boolean.opBoolean","MERGE",EDGE,{"derivedFrom":[makeQuery(id+"F16.boolean.opBoolean","SPLIT",EDGE,{"disambiguationData":[TD([makeQuery(id+"F16.opExtrude","SWEPT_FACE",FACE,{"disambiguationData":[OSD([subQ7])]})])],"derivedFrom":subQ37}),makeQuery(id+"F18.opExtrude","SWEPT_EDGE",EDGE,{"disambiguationData":[OSD([subQ2,subQ1,subQ0]),TDD([subQ3])]})]}),makeQuery(id+"F35.opExtrude","SWEPT_EDGE",EDGE,{"disambiguationData":[OSD([subQ2,subQ7,subQ6]),TDD([subQ8])]})]}),makeQuery(id+"F43.opExtrude","SWEPT_EDGE",EDGE,{"disambiguationData":[OSD([subQ2,subQ1,subQ0]),TDD([subQ4])]})]}),makeQuery(id+"F52.opExtrude","SWEPT_EDGE",EDGE,{"disambiguationData":[OSD([subQ2,subQ1,subQ0]),TDD([subQ5])]})]}),makeQuery(id+"F56.opExtrude","SWEPT_EDGE",EDGE,{"disambiguationData":[OSD([subQ2,subQ7,subQ6]),TDD([makeQuery(id+"F53.opExtrude","CAP_VERTEX",VERTEX,{"disambiguationData":[OSD([subQ2,subQ7,subQ6]),TDD([makeQuery(id+"F44.opExtrude","CAP_VERTEX",VERTEX,{"disambiguationData":[OSD([subQ2,subQ7,subQ6]),TDD([makeQuery(id+"F36.opExtrude","CAP_VERTEX",VERTEX,{"disambiguationData":[OSD([subQ2,subQ7,subQ6]),TDD([makeQuery(id+"F35.boolean.opBoolean","COPY",VERTEX,{"derivedFrom":makeQuery(id+"F35.opExtrude","CAP_VERTEX",VERTEX,{"disambiguationData":[OSD([subQ2,subQ7,subQ6]),TDD([subQ8])],"isStart":false})})])],"isStart":false})])],"isStart":false})])],"isStart":false})])]})]}),makeQuery(id+"F58.opExtrude","SWEPT_EDGE",EDGE,{"disambiguationData":[OSD([subQ2,subQ1,subQ0]),TDD([makeQuery(id+"F52.boolean.opBoolean","COPY",VERTEX,{"derivedFrom":makeQuery(id+"F52.opExtrude","CAP_VERTEX",VERTEX,{"disambiguationData":[OSD([subQ2,subQ1,subQ0]),TDD([subQ5])],"isStart":false})})])]})]})])]})]});}
            fillet(context, id + "F63", {"entities" : qUnion([Q0]), "radius" : 3 * mm, "tangentPropagation" : true, "allowEdgeOverflow" : false});
        }
    });
